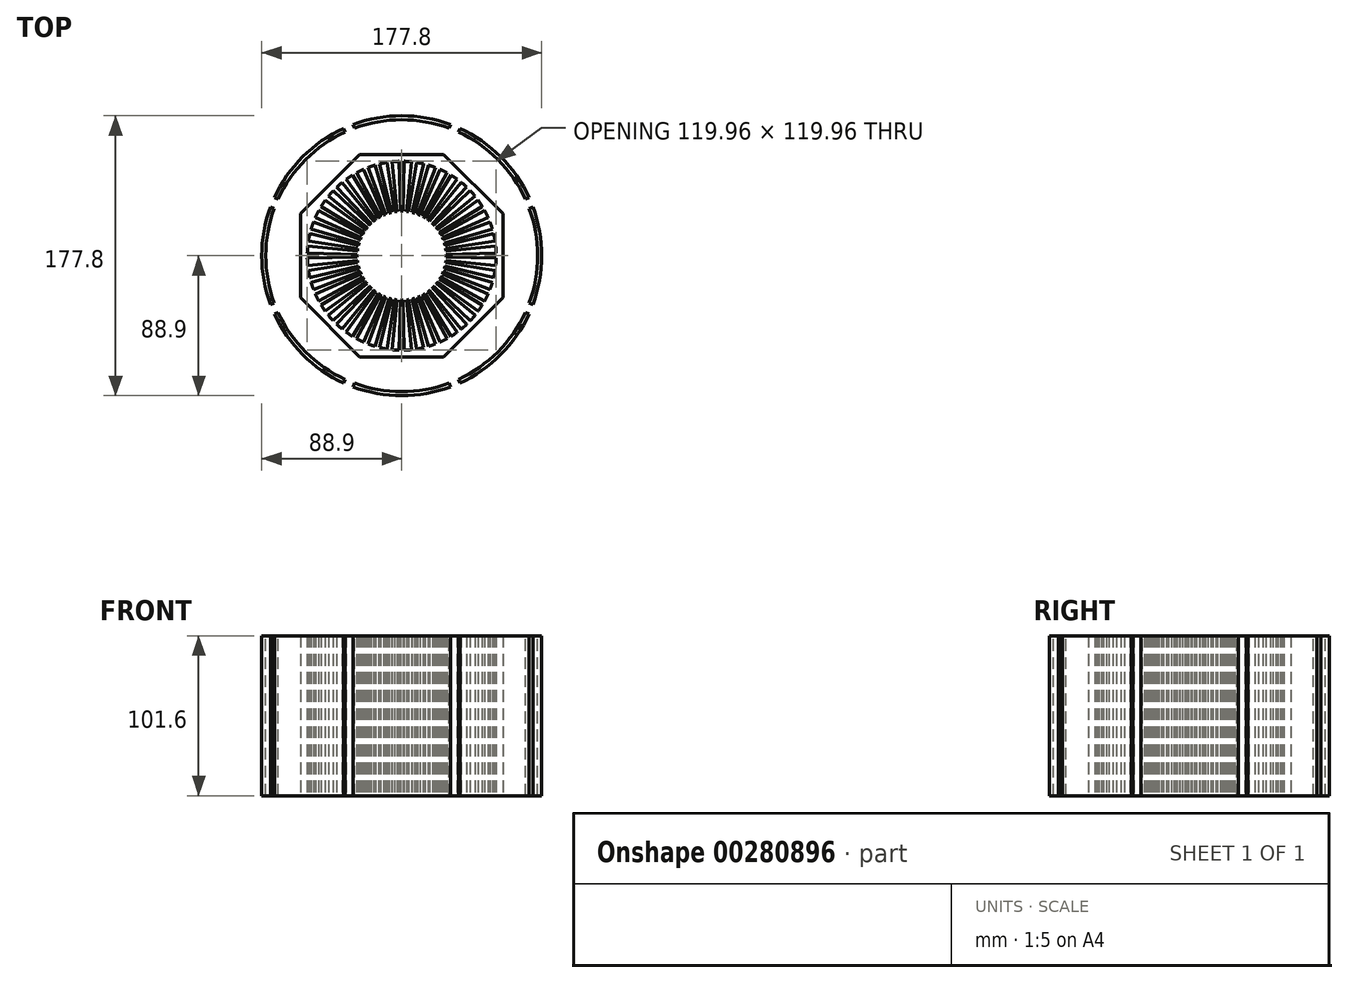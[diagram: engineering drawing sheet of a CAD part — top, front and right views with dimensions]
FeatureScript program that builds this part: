
annotation { "Feature Type Name" : "Feature", "Feature Type Description" : "" }
export const myFeature = defineFeature(function(context is Context, id is Id, definition is map)
    precondition{}
    {
        {
            var Q0;
            Q0=qCreatedBy(makeId("Top.planeOp"),FACE);
            var sketch = newSketch(context, id + "F0", { "sketchPlane" : qUnion([Q0])});
            skCircle(sketch, "E0", {"center": v(0, 0) * mm, "radius": 60 * mm});
            skCircle(sketch, "E1", {"center": v(0, 0) * mm, "radius": 457.2 * mm, "construction": true});
            skCircle(sketch, "E2.cCircle", {"center": v(0, 0) * mm, "radius": 64.39 * mm, "construction": true});
            skLineSegment(sketch, "E2.0", {"start": v(26.67, -64.39) * mm, "end": v(-26.67, -64.39) * mm});
            skLineSegment(sketch, "E2.1", {"start": v(-26.67, -64.39) * mm, "end": v(-64.39, -26.67) * mm});
            skLineSegment(sketch, "E2.2", {"start": v(-64.39, -26.67) * mm, "end": v(-64.39, 26.67) * mm});
            skLineSegment(sketch, "E2.3", {"start": v(-64.39, 26.67) * mm, "end": v(-26.67, 64.39) * mm});
            skLineSegment(sketch, "E2.4", {"start": v(-26.67, 64.39) * mm, "end": v(26.67, 64.39) * mm});
            skLineSegment(sketch, "E2.5", {"start": v(26.67, 64.39) * mm, "end": v(64.39, 26.67) * mm});
            skLineSegment(sketch, "E2.6", {"start": v(64.39, 26.67) * mm, "end": v(64.39, -26.67) * mm});
            skLineSegment(sketch, "E2.7", {"start": v(64.39, -26.67) * mm, "end": v(26.67, -64.39) * mm});
            skPoint(sketch, "E2.0.midPoint", {"position": v(0, -64.39) * mm});
            skLineSegment(sketch, "E3", {"start": v(0, 64.39) * mm, "end": v(0, 64.39) * mm});
            skPoint(sketch, "E3.endSnap0", {"position": v(0, 64.39) * mm});
            skPoint(sketch, "E4", {"position": v(-6.6, 64.39) * mm});
            skLineSegment(sketch, "E5", {"start": v(-6.6, 64.39) * mm, "end": v(-367.1, 272.52) * mm, "construction": true});
            skLineSegment(sketch, "E6.MirrorCS", {"start": v(6.6, 64.39) * mm, "end": v(367.1, 272.52) * mm, "construction": true});
            skLineSegment(sketch, "E7.bottom", {"start": v(114, -34) * mm, "end": v(-114, -34) * mm});
            skLineSegment(sketch, "E7.top", {"start": v(114, 34) * mm, "end": v(-114, 34) * mm});
            skLineSegment(sketch, "E7.left", {"start": v(114, -34) * mm, "end": v(114, 34) * mm});
            skLineSegment(sketch, "E7.right", {"start": v(-114, -34) * mm, "end": v(-114, 34) * mm});
            skCircle(sketch, "E8", {"center": v(0, 0) * mm, "radius": 88.9 * mm});
            skLineSegment(sketch, "E9", {"start": v(-26.67, 64.39) * mm, "end": v(-50.86, 122.8) * mm, "construction": true});
            skLineSegment(sketch, "E10.1.0", {"start": v(-50.2, 40.86) * mm, "end": v(-452.28, -66.88) * mm, "construction": true});
            skLineSegment(sketch, "E10.1.1", {"start": v(-40.86, 50.2) * mm, "end": v(66.88, 452.28) * mm, "construction": true});
            skLineSegment(sketch, "E10.2.0", {"start": v(-64.39, -6.6) * mm, "end": v(-272.52, -367.1) * mm, "construction": true});
            skLineSegment(sketch, "E10.2.1", {"start": v(-64.39, 6.6) * mm, "end": v(-272.52, 367.1) * mm, "construction": true});
            skLineSegment(sketch, "E10.3.0", {"start": v(-40.86, -50.2) * mm, "end": v(66.88, -452.28) * mm, "construction": true});
            skLineSegment(sketch, "E10.3.1", {"start": v(-50.2, -40.86) * mm, "end": v(-452.28, 66.88) * mm, "construction": true});
            skLineSegment(sketch, "E10.4.0", {"start": v(6.6, -64.39) * mm, "end": v(367.1, -272.52) * mm, "construction": true});
            skLineSegment(sketch, "E10.4.1", {"start": v(-6.6, -64.39) * mm, "end": v(-367.1, -272.52) * mm, "construction": true});
            skLineSegment(sketch, "E10.5.0", {"start": v(50.2, -40.86) * mm, "end": v(452.28, 66.88) * mm, "construction": true});
            skLineSegment(sketch, "E10.5.1", {"start": v(40.86, -50.2) * mm, "end": v(-66.88, -452.28) * mm, "construction": true});
            skLineSegment(sketch, "E10.6.0", {"start": v(64.39, 6.6) * mm, "end": v(272.52, 367.1) * mm, "construction": true});
            skLineSegment(sketch, "E10.6.1", {"start": v(64.39, -6.6) * mm, "end": v(272.52, -367.1) * mm, "construction": true});
            skLineSegment(sketch, "E10.7.0", {"start": v(40.86, 50.2) * mm, "end": v(-66.88, 452.28) * mm, "construction": true});
            skLineSegment(sketch, "E10.7.1", {"start": v(50.2, 40.86) * mm, "end": v(452.28, -66.88) * mm, "construction": true});
            skPoint(sketch, "E11", {"position": v(-32.98, 79.62) * mm});
            skLineSegment(sketch, "E12", {"start": v(0, -64.39) * mm, "end": v(0, -133.64) * mm, "construction": true});
            skSolve(sketch);
        }
        {
            var Q0;
            Q0=qCreatedBy(makeId("Top.planeOp"),FACE);
            var sketch = newSketch(context, id + "F1", { "sketchPlane" : qUnion([Q0])});
            skLineSegment(sketch, "E13.0", {"start": v(-26.67, 64.39) * mm, "end": v(26.67, 64.39) * mm});
            skLineSegment(sketch, "E14.0", {"start": v(-64.39, 26.67) * mm, "end": v(-26.67, 64.39) * mm});
            skLineSegment(sketch, "E15.0", {"start": v(-64.39, -26.67) * mm, "end": v(-64.39, 26.67) * mm});
            skLineSegment(sketch, "E16.0", {"start": v(-26.67, -64.39) * mm, "end": v(-64.39, -26.67) * mm});
            skLineSegment(sketch, "E17.0", {"start": v(26.67, -64.39) * mm, "end": v(-26.67, -64.39) * mm});
            skLineSegment(sketch, "E18.0", {"start": v(64.39, -26.67) * mm, "end": v(26.67, -64.39) * mm});
            skLineSegment(sketch, "E19.0", {"start": v(64.39, 26.67) * mm, "end": v(64.39, -26.67) * mm});
            skLineSegment(sketch, "E20.0", {"start": v(26.67, 64.39) * mm, "end": v(64.39, 26.67) * mm});
            skCircle(sketch, "E21.0", {"center": v(0, 0) * mm, "radius": 60 * mm});
            skSolve(sketch);
        }
        {
            var Q0;
            Q0 = qSketchRegion(id + "F1", true);
            extrude(context, id + "F2", {"entities" : qUnion([Q0]), "endBound" : BoundingType.SYMMETRIC, "depth" : 101.6 * mm});
        }
        {
            var Q0;
            Q0=qCreatedBy(makeId("Top.planeOp"),FACE);
            var sketch = newSketch(context, id + "F3", { "sketchPlane" : qUnion([Q0])});
            skArc(sketch, "E22", {"start": v(0.74, 28.24) * mm, "mid": v(0, 28.25) * mm, "end": v(-0.74, 28.24) * mm});
            skArc(sketch, "E23.0", {"start": v(1.57, 59.98) * mm, "mid": v(0, 60) * mm, "end": v(-1.57, 59.98) * mm});
            skLineSegment(sketch, "E24", {"start": v(0, 0) * mm, "end": v(0, 69.36) * mm, "construction": true});
            skLineSegment(sketch, "E25", {"start": v(-0.74, 28.24) * mm, "end": v(-1.57, 59.98) * mm});
            skLineSegment(sketch, "E26.MirrorCS", {"start": v(0.74, 28.24) * mm, "end": v(1.57, 59.98) * mm});
            skLineSegment(sketch, "E27.1.0", {"start": v(-4.42, 27.9) * mm, "end": v(-9.39, 59.26) * mm});
            skLineSegment(sketch, "E27.1.1", {"start": v(-2.95, 28.1) * mm, "end": v(-6.27, 59.67) * mm});
            skArc(sketch, "E27.1.2", {"start": v(-2.95, 28.1) * mm, "mid": v(-3.69, 28) * mm, "end": v(-4.42, 27.9) * mm});
            skArc(sketch, "E27.1.3", {"start": v(-6.27, 59.67) * mm, "mid": v(-7.83, 59.49) * mm, "end": v(-9.39, 59.26) * mm});
            skLineSegment(sketch, "E27.2.0", {"start": v(-8.02, 27.09) * mm, "end": v(-17.04, 57.53) * mm});
            skLineSegment(sketch, "E27.2.1", {"start": v(-6.6, 27.47) * mm, "end": v(-14, 58.34) * mm});
            skArc(sketch, "E27.2.2", {"start": v(-6.6, 27.47) * mm, "mid": v(-7.31, 27.29) * mm, "end": v(-8.02, 27.09) * mm});
            skArc(sketch, "E27.2.3", {"start": v(-14, 58.34) * mm, "mid": v(-15.53, 57.96) * mm, "end": v(-17.04, 57.53) * mm});
            skLineSegment(sketch, "E27.3.0", {"start": v(-11.5, 25.8) * mm, "end": v(-24.4, 54.81) * mm});
            skLineSegment(sketch, "E27.3.1", {"start": v(-10.12, 26.37) * mm, "end": v(-21.5, 56.01) * mm});
            skArc(sketch, "E27.3.2", {"start": v(-10.12, 26.37) * mm, "mid": v(-10.81, 26.1) * mm, "end": v(-11.5, 25.8) * mm});
            skArc(sketch, "E27.3.3", {"start": v(-21.5, 56.01) * mm, "mid": v(-22.96, 55.43) * mm, "end": v(-24.4, 54.81) * mm});
            skLineSegment(sketch, "E27.4.0", {"start": v(-14.76, 24.09) * mm, "end": v(-31.35, 51.16) * mm});
            skLineSegment(sketch, "E27.4.1", {"start": v(-13.48, 24.83) * mm, "end": v(-28.63, 52.73) * mm});
            skArc(sketch, "E27.4.2", {"start": v(-13.48, 24.83) * mm, "mid": v(-14.13, 24.47) * mm, "end": v(-14.76, 24.09) * mm});
            skArc(sketch, "E27.4.3", {"start": v(-28.63, 52.73) * mm, "mid": v(-30, 51.96) * mm, "end": v(-31.35, 51.16) * mm});
            skLineSegment(sketch, "E27.5.0", {"start": v(-17.78, 21.95) * mm, "end": v(-37.76, 46.63) * mm});
            skLineSegment(sketch, "E27.5.1", {"start": v(-16.6, 22.85) * mm, "end": v(-35.27, 48.54) * mm});
            skArc(sketch, "E27.5.2", {"start": v(-16.6, 22.85) * mm, "mid": v(-17.2, 22.41) * mm, "end": v(-17.78, 21.95) * mm});
            skArc(sketch, "E27.5.3", {"start": v(-35.27, 48.54) * mm, "mid": v(-36.53, 47.6) * mm, "end": v(-37.76, 46.63) * mm});
            skLineSegment(sketch, "E27.6.0", {"start": v(-20.5, 19.45) * mm, "end": v(-43.52, 41.3) * mm});
            skLineSegment(sketch, "E27.6.1", {"start": v(-19.45, 20.5) * mm, "end": v(-41.3, 43.52) * mm});
            skArc(sketch, "E27.6.2", {"start": v(-19.45, 20.5) * mm, "mid": v(-19.98, 19.98) * mm, "end": v(-20.5, 19.45) * mm});
            skArc(sketch, "E27.6.3", {"start": v(-41.3, 43.52) * mm, "mid": v(-42.43, 42.43) * mm, "end": v(-43.52, 41.3) * mm});
            skLineSegment(sketch, "E27.7.0", {"start": v(-22.85, 16.6) * mm, "end": v(-48.54, 35.27) * mm});
            skLineSegment(sketch, "E27.7.1", {"start": v(-21.95, 17.78) * mm, "end": v(-46.63, 37.76) * mm});
            skArc(sketch, "E27.7.2", {"start": v(-21.95, 17.78) * mm, "mid": v(-22.41, 17.2) * mm, "end": v(-22.85, 16.6) * mm});
            skArc(sketch, "E27.7.3", {"start": v(-46.63, 37.76) * mm, "mid": v(-47.6, 36.53) * mm, "end": v(-48.54, 35.27) * mm});
            skLineSegment(sketch, "E27.8.0", {"start": v(-24.83, 13.48) * mm, "end": v(-52.73, 28.63) * mm});
            skLineSegment(sketch, "E27.8.1", {"start": v(-24.09, 14.76) * mm, "end": v(-51.16, 31.35) * mm});
            skArc(sketch, "E27.8.2", {"start": v(-24.09, 14.76) * mm, "mid": v(-24.47, 14.12) * mm, "end": v(-24.83, 13.48) * mm});
            skArc(sketch, "E27.8.3", {"start": v(-51.16, 31.35) * mm, "mid": v(-51.96, 30) * mm, "end": v(-52.73, 28.63) * mm});
            skLineSegment(sketch, "E27.9.0", {"start": v(-26.37, 10.12) * mm, "end": v(-56.01, 21.5) * mm});
            skLineSegment(sketch, "E27.9.1", {"start": v(-25.8, 11.5) * mm, "end": v(-54.81, 24.4) * mm});
            skArc(sketch, "E27.9.2", {"start": v(-25.8, 11.5) * mm, "mid": v(-26.1, 10.81) * mm, "end": v(-26.37, 10.12) * mm});
            skArc(sketch, "E27.9.3", {"start": v(-54.81, 24.4) * mm, "mid": v(-55.43, 22.96) * mm, "end": v(-56.01, 21.5) * mm});
            skLineSegment(sketch, "E27.10.0", {"start": v(-27.47, 6.6) * mm, "end": v(-58.34, 14) * mm});
            skLineSegment(sketch, "E27.10.1", {"start": v(-27.09, 8.02) * mm, "end": v(-57.53, 17.04) * mm});
            skArc(sketch, "E27.10.2", {"start": v(-27.09, 8.02) * mm, "mid": v(-27.29, 7.31) * mm, "end": v(-27.47, 6.6) * mm});
            skArc(sketch, "E27.10.3", {"start": v(-57.53, 17.04) * mm, "mid": v(-57.96, 15.53) * mm, "end": v(-58.34, 14) * mm});
            skLineSegment(sketch, "E27.11.0", {"start": v(-28.1, 2.95) * mm, "end": v(-59.67, 6.27) * mm});
            skLineSegment(sketch, "E27.11.1", {"start": v(-27.9, 4.42) * mm, "end": v(-59.26, 9.39) * mm});
            skArc(sketch, "E27.11.2", {"start": v(-27.9, 4.42) * mm, "mid": v(-28, 3.69) * mm, "end": v(-28.1, 2.95) * mm});
            skArc(sketch, "E27.11.3", {"start": v(-59.26, 9.39) * mm, "mid": v(-59.49, 7.83) * mm, "end": v(-59.67, 6.27) * mm});
            skLineSegment(sketch, "E27.12.0", {"start": v(-28.24, -0.74) * mm, "end": v(-59.98, -1.57) * mm});
            skLineSegment(sketch, "E27.12.1", {"start": v(-28.24, 0.74) * mm, "end": v(-59.98, 1.57) * mm});
            skArc(sketch, "E27.12.2", {"start": v(-28.24, 0.74) * mm, "mid": v(-28.25, 0) * mm, "end": v(-28.24, -0.74) * mm});
            skArc(sketch, "E27.12.3", {"start": v(-59.98, 1.57) * mm, "mid": v(-60, 0) * mm, "end": v(-59.98, -1.57) * mm});
            skLineSegment(sketch, "E27.13.0", {"start": v(-27.9, -4.42) * mm, "end": v(-59.26, -9.39) * mm});
            skLineSegment(sketch, "E27.13.1", {"start": v(-28.1, -2.95) * mm, "end": v(-59.67, -6.27) * mm});
            skArc(sketch, "E27.13.2", {"start": v(-28.1, -2.95) * mm, "mid": v(-28, -3.69) * mm, "end": v(-27.9, -4.42) * mm});
            skArc(sketch, "E27.13.3", {"start": v(-59.67, -6.27) * mm, "mid": v(-59.49, -7.83) * mm, "end": v(-59.26, -9.39) * mm});
            skLineSegment(sketch, "E27.14.0", {"start": v(-27.09, -8.02) * mm, "end": v(-57.53, -17.04) * mm});
            skLineSegment(sketch, "E27.14.1", {"start": v(-27.47, -6.6) * mm, "end": v(-58.34, -14) * mm});
            skArc(sketch, "E27.14.2", {"start": v(-27.47, -6.6) * mm, "mid": v(-27.29, -7.31) * mm, "end": v(-27.09, -8.02) * mm});
            skArc(sketch, "E27.14.3", {"start": v(-58.34, -14) * mm, "mid": v(-57.96, -15.53) * mm, "end": v(-57.53, -17.04) * mm});
            skLineSegment(sketch, "E27.15.0", {"start": v(-25.8, -11.5) * mm, "end": v(-54.81, -24.4) * mm});
            skLineSegment(sketch, "E27.15.1", {"start": v(-26.37, -10.12) * mm, "end": v(-56.01, -21.5) * mm});
            skArc(sketch, "E27.15.2", {"start": v(-26.37, -10.12) * mm, "mid": v(-26.1, -10.81) * mm, "end": v(-25.8, -11.5) * mm});
            skArc(sketch, "E27.15.3", {"start": v(-56.01, -21.5) * mm, "mid": v(-55.43, -22.96) * mm, "end": v(-54.81, -24.4) * mm});
            skLineSegment(sketch, "E27.16.0", {"start": v(-24.09, -14.76) * mm, "end": v(-51.16, -31.35) * mm});
            skLineSegment(sketch, "E27.16.1", {"start": v(-24.83, -13.48) * mm, "end": v(-52.73, -28.63) * mm});
            skArc(sketch, "E27.16.2", {"start": v(-24.83, -13.48) * mm, "mid": v(-24.47, -14.13) * mm, "end": v(-24.09, -14.76) * mm});
            skArc(sketch, "E27.16.3", {"start": v(-52.73, -28.63) * mm, "mid": v(-51.96, -30) * mm, "end": v(-51.16, -31.35) * mm});
            skLineSegment(sketch, "E27.17.0", {"start": v(-21.95, -17.78) * mm, "end": v(-46.63, -37.76) * mm});
            skLineSegment(sketch, "E27.17.1", {"start": v(-22.85, -16.6) * mm, "end": v(-48.54, -35.27) * mm});
            skArc(sketch, "E27.17.2", {"start": v(-22.85, -16.6) * mm, "mid": v(-22.41, -17.2) * mm, "end": v(-21.95, -17.78) * mm});
            skArc(sketch, "E27.17.3", {"start": v(-48.54, -35.27) * mm, "mid": v(-47.6, -36.53) * mm, "end": v(-46.63, -37.76) * mm});
            skLineSegment(sketch, "E27.18.0", {"start": v(-19.45, -20.5) * mm, "end": v(-41.3, -43.52) * mm});
            skLineSegment(sketch, "E27.18.1", {"start": v(-20.5, -19.45) * mm, "end": v(-43.52, -41.3) * mm});
            skArc(sketch, "E27.18.2", {"start": v(-20.5, -19.45) * mm, "mid": v(-19.98, -19.98) * mm, "end": v(-19.45, -20.5) * mm});
            skArc(sketch, "E27.18.3", {"start": v(-43.52, -41.3) * mm, "mid": v(-42.43, -42.43) * mm, "end": v(-41.3, -43.52) * mm});
            skLineSegment(sketch, "E27.19.0", {"start": v(-16.6, -22.85) * mm, "end": v(-35.27, -48.54) * mm});
            skLineSegment(sketch, "E27.19.1", {"start": v(-17.78, -21.95) * mm, "end": v(-37.76, -46.63) * mm});
            skArc(sketch, "E27.19.2", {"start": v(-17.78, -21.95) * mm, "mid": v(-17.2, -22.41) * mm, "end": v(-16.6, -22.85) * mm});
            skArc(sketch, "E27.19.3", {"start": v(-37.76, -46.63) * mm, "mid": v(-36.53, -47.6) * mm, "end": v(-35.27, -48.54) * mm});
            skLineSegment(sketch, "E27.20.0", {"start": v(-13.48, -24.83) * mm, "end": v(-28.63, -52.73) * mm});
            skLineSegment(sketch, "E27.20.1", {"start": v(-14.76, -24.09) * mm, "end": v(-31.35, -51.16) * mm});
            skArc(sketch, "E27.20.2", {"start": v(-14.76, -24.09) * mm, "mid": v(-14.12, -24.47) * mm, "end": v(-13.48, -24.83) * mm});
            skArc(sketch, "E27.20.3", {"start": v(-31.35, -51.16) * mm, "mid": v(-30, -51.96) * mm, "end": v(-28.63, -52.73) * mm});
            skLineSegment(sketch, "E27.21.0", {"start": v(-10.12, -26.37) * mm, "end": v(-21.5, -56.01) * mm});
            skLineSegment(sketch, "E27.21.1", {"start": v(-11.5, -25.8) * mm, "end": v(-24.4, -54.81) * mm});
            skArc(sketch, "E27.21.2", {"start": v(-11.5, -25.8) * mm, "mid": v(-10.81, -26.1) * mm, "end": v(-10.12, -26.37) * mm});
            skArc(sketch, "E27.21.3", {"start": v(-24.4, -54.81) * mm, "mid": v(-22.96, -55.43) * mm, "end": v(-21.5, -56.01) * mm});
            skLineSegment(sketch, "E27.22.0", {"start": v(-6.6, -27.47) * mm, "end": v(-14, -58.34) * mm});
            skLineSegment(sketch, "E27.22.1", {"start": v(-8.02, -27.09) * mm, "end": v(-17.04, -57.53) * mm});
            skArc(sketch, "E27.22.2", {"start": v(-8.02, -27.09) * mm, "mid": v(-7.31, -27.29) * mm, "end": v(-6.6, -27.47) * mm});
            skArc(sketch, "E27.22.3", {"start": v(-17.04, -57.53) * mm, "mid": v(-15.53, -57.96) * mm, "end": v(-14, -58.34) * mm});
            skLineSegment(sketch, "E27.23.0", {"start": v(-2.95, -28.1) * mm, "end": v(-6.27, -59.67) * mm});
            skLineSegment(sketch, "E27.23.1", {"start": v(-4.42, -27.9) * mm, "end": v(-9.39, -59.26) * mm});
            skArc(sketch, "E27.23.2", {"start": v(-4.42, -27.9) * mm, "mid": v(-3.69, -28) * mm, "end": v(-2.95, -28.1) * mm});
            skArc(sketch, "E27.23.3", {"start": v(-9.39, -59.26) * mm, "mid": v(-7.83, -59.49) * mm, "end": v(-6.27, -59.67) * mm});
            skLineSegment(sketch, "E27.24.0", {"start": v(0.74, -28.24) * mm, "end": v(1.57, -59.98) * mm});
            skLineSegment(sketch, "E27.24.1", {"start": v(-0.74, -28.24) * mm, "end": v(-1.57, -59.98) * mm});
            skArc(sketch, "E27.24.2", {"start": v(-0.74, -28.24) * mm, "mid": v(0, -28.25) * mm, "end": v(0.74, -28.24) * mm});
            skArc(sketch, "E27.24.3", {"start": v(-1.57, -59.98) * mm, "mid": v(0, -60) * mm, "end": v(1.57, -59.98) * mm});
            skLineSegment(sketch, "E27.25.0", {"start": v(4.42, -27.9) * mm, "end": v(9.39, -59.26) * mm});
            skLineSegment(sketch, "E27.25.1", {"start": v(2.95, -28.1) * mm, "end": v(6.27, -59.67) * mm});
            skArc(sketch, "E27.25.2", {"start": v(2.95, -28.1) * mm, "mid": v(3.69, -28) * mm, "end": v(4.42, -27.9) * mm});
            skArc(sketch, "E27.25.3", {"start": v(6.27, -59.67) * mm, "mid": v(7.83, -59.49) * mm, "end": v(9.39, -59.26) * mm});
            skLineSegment(sketch, "E27.26.0", {"start": v(8.02, -27.09) * mm, "end": v(17.04, -57.53) * mm});
            skLineSegment(sketch, "E27.26.1", {"start": v(6.6, -27.47) * mm, "end": v(14, -58.34) * mm});
            skArc(sketch, "E27.26.2", {"start": v(6.6, -27.47) * mm, "mid": v(7.31, -27.29) * mm, "end": v(8.02, -27.09) * mm});
            skArc(sketch, "E27.26.3", {"start": v(14, -58.34) * mm, "mid": v(15.53, -57.96) * mm, "end": v(17.04, -57.53) * mm});
            skLineSegment(sketch, "E27.27.0", {"start": v(11.5, -25.8) * mm, "end": v(24.4, -54.81) * mm});
            skLineSegment(sketch, "E27.27.1", {"start": v(10.12, -26.37) * mm, "end": v(21.5, -56.01) * mm});
            skArc(sketch, "E27.27.2", {"start": v(10.12, -26.37) * mm, "mid": v(10.81, -26.1) * mm, "end": v(11.5, -25.8) * mm});
            skArc(sketch, "E27.27.3", {"start": v(21.5, -56.01) * mm, "mid": v(22.96, -55.43) * mm, "end": v(24.4, -54.81) * mm});
            skLineSegment(sketch, "E27.28.0", {"start": v(14.76, -24.09) * mm, "end": v(31.35, -51.16) * mm});
            skLineSegment(sketch, "E27.28.1", {"start": v(13.48, -24.83) * mm, "end": v(28.63, -52.73) * mm});
            skArc(sketch, "E27.28.2", {"start": v(13.48, -24.83) * mm, "mid": v(14.13, -24.47) * mm, "end": v(14.76, -24.09) * mm});
            skArc(sketch, "E27.28.3", {"start": v(28.63, -52.73) * mm, "mid": v(30, -51.96) * mm, "end": v(31.35, -51.16) * mm});
            skLineSegment(sketch, "E27.29.0", {"start": v(17.78, -21.95) * mm, "end": v(37.76, -46.63) * mm});
            skLineSegment(sketch, "E27.29.1", {"start": v(16.6, -22.85) * mm, "end": v(35.27, -48.54) * mm});
            skArc(sketch, "E27.29.2", {"start": v(16.6, -22.85) * mm, "mid": v(17.2, -22.41) * mm, "end": v(17.78, -21.95) * mm});
            skArc(sketch, "E27.29.3", {"start": v(35.27, -48.54) * mm, "mid": v(36.53, -47.6) * mm, "end": v(37.76, -46.63) * mm});
            skLineSegment(sketch, "E27.30.0", {"start": v(20.5, -19.45) * mm, "end": v(43.52, -41.3) * mm});
            skLineSegment(sketch, "E27.30.1", {"start": v(19.45, -20.5) * mm, "end": v(41.3, -43.52) * mm});
            skArc(sketch, "E27.30.2", {"start": v(19.45, -20.5) * mm, "mid": v(19.98, -19.98) * mm, "end": v(20.5, -19.45) * mm});
            skArc(sketch, "E27.30.3", {"start": v(41.3, -43.52) * mm, "mid": v(42.43, -42.43) * mm, "end": v(43.52, -41.3) * mm});
            skLineSegment(sketch, "E27.31.0", {"start": v(22.85, -16.6) * mm, "end": v(48.54, -35.27) * mm});
            skLineSegment(sketch, "E27.31.1", {"start": v(21.95, -17.78) * mm, "end": v(46.63, -37.76) * mm});
            skArc(sketch, "E27.31.2", {"start": v(21.95, -17.78) * mm, "mid": v(22.41, -17.2) * mm, "end": v(22.85, -16.6) * mm});
            skArc(sketch, "E27.31.3", {"start": v(46.63, -37.76) * mm, "mid": v(47.6, -36.53) * mm, "end": v(48.54, -35.27) * mm});
            skLineSegment(sketch, "E27.32.0", {"start": v(24.83, -13.48) * mm, "end": v(52.73, -28.63) * mm});
            skLineSegment(sketch, "E27.32.1", {"start": v(24.09, -14.76) * mm, "end": v(51.16, -31.35) * mm});
            skArc(sketch, "E27.32.2", {"start": v(24.09, -14.76) * mm, "mid": v(24.47, -14.13) * mm, "end": v(24.83, -13.48) * mm});
            skArc(sketch, "E27.32.3", {"start": v(51.16, -31.35) * mm, "mid": v(51.96, -30) * mm, "end": v(52.73, -28.63) * mm});
            skLineSegment(sketch, "E27.33.0", {"start": v(26.37, -10.12) * mm, "end": v(56.01, -21.5) * mm});
            skLineSegment(sketch, "E27.33.1", {"start": v(25.8, -11.5) * mm, "end": v(54.81, -24.4) * mm});
            skArc(sketch, "E27.33.2", {"start": v(25.8, -11.5) * mm, "mid": v(26.1, -10.81) * mm, "end": v(26.37, -10.12) * mm});
            skArc(sketch, "E27.33.3", {"start": v(54.81, -24.4) * mm, "mid": v(55.43, -22.96) * mm, "end": v(56.01, -21.5) * mm});
            skLineSegment(sketch, "E27.34.0", {"start": v(27.47, -6.6) * mm, "end": v(58.34, -14) * mm});
            skLineSegment(sketch, "E27.34.1", {"start": v(27.09, -8.02) * mm, "end": v(57.53, -17.04) * mm});
            skArc(sketch, "E27.34.2", {"start": v(27.09, -8.02) * mm, "mid": v(27.29, -7.31) * mm, "end": v(27.47, -6.6) * mm});
            skArc(sketch, "E27.34.3", {"start": v(57.53, -17.04) * mm, "mid": v(57.96, -15.53) * mm, "end": v(58.34, -14) * mm});
            skLineSegment(sketch, "E27.35.0", {"start": v(28.1, -2.95) * mm, "end": v(59.67, -6.27) * mm});
            skLineSegment(sketch, "E27.35.1", {"start": v(27.9, -4.42) * mm, "end": v(59.26, -9.39) * mm});
            skArc(sketch, "E27.35.2", {"start": v(27.9, -4.42) * mm, "mid": v(28, -3.69) * mm, "end": v(28.1, -2.95) * mm});
            skArc(sketch, "E27.35.3", {"start": v(59.26, -9.39) * mm, "mid": v(59.49, -7.83) * mm, "end": v(59.67, -6.27) * mm});
            skLineSegment(sketch, "E27.36.0", {"start": v(28.24, 0.74) * mm, "end": v(59.98, 1.57) * mm});
            skLineSegment(sketch, "E27.36.1", {"start": v(28.24, -0.74) * mm, "end": v(59.98, -1.57) * mm});
            skArc(sketch, "E27.36.2", {"start": v(28.24, -0.74) * mm, "mid": v(28.25, 0) * mm, "end": v(28.24, 0.74) * mm});
            skArc(sketch, "E27.36.3", {"start": v(59.98, -1.57) * mm, "mid": v(60, 0) * mm, "end": v(59.98, 1.57) * mm});
            skLineSegment(sketch, "E27.37.0", {"start": v(27.9, 4.42) * mm, "end": v(59.26, 9.39) * mm});
            skLineSegment(sketch, "E27.37.1", {"start": v(28.1, 2.95) * mm, "end": v(59.67, 6.27) * mm});
            skArc(sketch, "E27.37.2", {"start": v(28.1, 2.95) * mm, "mid": v(28, 3.69) * mm, "end": v(27.9, 4.42) * mm});
            skArc(sketch, "E27.37.3", {"start": v(59.67, 6.27) * mm, "mid": v(59.49, 7.83) * mm, "end": v(59.26, 9.39) * mm});
            skLineSegment(sketch, "E27.38.0", {"start": v(27.09, 8.02) * mm, "end": v(57.53, 17.04) * mm});
            skLineSegment(sketch, "E27.38.1", {"start": v(27.47, 6.6) * mm, "end": v(58.34, 14) * mm});
            skArc(sketch, "E27.38.2", {"start": v(27.47, 6.6) * mm, "mid": v(27.29, 7.31) * mm, "end": v(27.09, 8.02) * mm});
            skArc(sketch, "E27.38.3", {"start": v(58.34, 14) * mm, "mid": v(57.96, 15.53) * mm, "end": v(57.53, 17.04) * mm});
            skLineSegment(sketch, "E27.39.0", {"start": v(25.8, 11.5) * mm, "end": v(54.81, 24.4) * mm});
            skLineSegment(sketch, "E27.39.1", {"start": v(26.37, 10.12) * mm, "end": v(56.01, 21.5) * mm});
            skArc(sketch, "E27.39.2", {"start": v(26.37, 10.12) * mm, "mid": v(26.1, 10.81) * mm, "end": v(25.8, 11.5) * mm});
            skArc(sketch, "E27.39.3", {"start": v(56.01, 21.5) * mm, "mid": v(55.43, 22.96) * mm, "end": v(54.81, 24.4) * mm});
            skLineSegment(sketch, "E27.40.0", {"start": v(24.09, 14.76) * mm, "end": v(51.16, 31.35) * mm});
            skLineSegment(sketch, "E27.40.1", {"start": v(24.83, 13.48) * mm, "end": v(52.73, 28.63) * mm});
            skArc(sketch, "E27.40.2", {"start": v(24.83, 13.48) * mm, "mid": v(24.47, 14.12) * mm, "end": v(24.09, 14.76) * mm});
            skArc(sketch, "E27.40.3", {"start": v(52.73, 28.63) * mm, "mid": v(51.96, 30) * mm, "end": v(51.16, 31.35) * mm});
            skLineSegment(sketch, "E27.41.0", {"start": v(21.95, 17.78) * mm, "end": v(46.63, 37.76) * mm});
            skLineSegment(sketch, "E27.41.1", {"start": v(22.85, 16.6) * mm, "end": v(48.54, 35.27) * mm});
            skArc(sketch, "E27.41.2", {"start": v(22.85, 16.6) * mm, "mid": v(22.41, 17.2) * mm, "end": v(21.95, 17.78) * mm});
            skArc(sketch, "E27.41.3", {"start": v(48.54, 35.27) * mm, "mid": v(47.6, 36.53) * mm, "end": v(46.63, 37.76) * mm});
            skLineSegment(sketch, "E27.42.0", {"start": v(19.45, 20.5) * mm, "end": v(41.3, 43.52) * mm});
            skLineSegment(sketch, "E27.42.1", {"start": v(20.5, 19.45) * mm, "end": v(43.52, 41.3) * mm});
            skArc(sketch, "E27.42.2", {"start": v(20.5, 19.45) * mm, "mid": v(19.98, 19.98) * mm, "end": v(19.45, 20.5) * mm});
            skArc(sketch, "E27.42.3", {"start": v(43.52, 41.3) * mm, "mid": v(42.43, 42.43) * mm, "end": v(41.3, 43.52) * mm});
            skLineSegment(sketch, "E27.43.0", {"start": v(16.6, 22.85) * mm, "end": v(35.27, 48.54) * mm});
            skLineSegment(sketch, "E27.43.1", {"start": v(17.78, 21.95) * mm, "end": v(37.76, 46.63) * mm});
            skArc(sketch, "E27.43.2", {"start": v(17.78, 21.95) * mm, "mid": v(17.2, 22.41) * mm, "end": v(16.6, 22.85) * mm});
            skArc(sketch, "E27.43.3", {"start": v(37.76, 46.63) * mm, "mid": v(36.53, 47.6) * mm, "end": v(35.27, 48.54) * mm});
            skLineSegment(sketch, "E27.44.0", {"start": v(13.48, 24.83) * mm, "end": v(28.63, 52.73) * mm});
            skLineSegment(sketch, "E27.44.1", {"start": v(14.76, 24.09) * mm, "end": v(31.35, 51.16) * mm});
            skArc(sketch, "E27.44.2", {"start": v(14.76, 24.09) * mm, "mid": v(14.13, 24.47) * mm, "end": v(13.48, 24.83) * mm});
            skArc(sketch, "E27.44.3", {"start": v(31.35, 51.16) * mm, "mid": v(30, 51.96) * mm, "end": v(28.63, 52.73) * mm});
            skLineSegment(sketch, "E27.45.0", {"start": v(10.12, 26.37) * mm, "end": v(21.5, 56.01) * mm});
            skLineSegment(sketch, "E27.45.1", {"start": v(11.5, 25.8) * mm, "end": v(24.4, 54.81) * mm});
            skArc(sketch, "E27.45.2", {"start": v(11.5, 25.8) * mm, "mid": v(10.81, 26.1) * mm, "end": v(10.12, 26.37) * mm});
            skArc(sketch, "E27.45.3", {"start": v(24.4, 54.81) * mm, "mid": v(22.96, 55.43) * mm, "end": v(21.5, 56.01) * mm});
            skLineSegment(sketch, "E27.46.0", {"start": v(6.6, 27.47) * mm, "end": v(14, 58.34) * mm});
            skLineSegment(sketch, "E27.46.1", {"start": v(8.02, 27.09) * mm, "end": v(17.04, 57.53) * mm});
            skArc(sketch, "E27.46.2", {"start": v(8.02, 27.09) * mm, "mid": v(7.31, 27.29) * mm, "end": v(6.6, 27.47) * mm});
            skArc(sketch, "E27.46.3", {"start": v(17.04, 57.53) * mm, "mid": v(15.53, 57.96) * mm, "end": v(14, 58.34) * mm});
            skLineSegment(sketch, "E27.47.0", {"start": v(2.95, 28.1) * mm, "end": v(6.27, 59.67) * mm});
            skLineSegment(sketch, "E27.47.1", {"start": v(4.42, 27.9) * mm, "end": v(9.39, 59.26) * mm});
            skArc(sketch, "E27.47.2", {"start": v(4.42, 27.9) * mm, "mid": v(3.69, 28) * mm, "end": v(2.95, 28.1) * mm});
            skArc(sketch, "E27.47.3", {"start": v(9.39, 59.26) * mm, "mid": v(7.83, 59.49) * mm, "end": v(6.27, 59.67) * mm});
            skSolve(sketch);
        }
        {
            var Q0;
            Q0 = qSketchRegion(id + "F3", true);
            var Q1;
            Q1=makeQuery(id+"F2.opExtrude","CAP_FACE",FACE,{"disambiguationData":[OSD([sQuery(id+"F1.wireOp",EDGE,"E13.0"),sQuery(id+"F1.wireOp",EDGE,"E14.0"),sQuery(id+"F1.wireOp",EDGE,"E15.0"),sQuery(id+"F1.wireOp",EDGE,"E16.0"),sQuery(id+"F1.wireOp",EDGE,"E17.0"),sQuery(id+"F1.wireOp",EDGE,"E18.0"),sQuery(id+"F1.wireOp",EDGE,"E19.0"),sQuery(id+"F1.wireOp",EDGE,"E20.0"),sQuery(id+"F1.wireOp",EDGE,"E21.0")])],"isStart":false});
            var Q2;
            Q2=makeQuery(id+"F2.opExtrude","CAP_FACE",FACE,{"disambiguationData":[OSD([sQuery(id+"F1.wireOp",EDGE,"E13.0"),sQuery(id+"F1.wireOp",EDGE,"E14.0"),sQuery(id+"F1.wireOp",EDGE,"E15.0"),sQuery(id+"F1.wireOp",EDGE,"E16.0"),sQuery(id+"F1.wireOp",EDGE,"E17.0"),sQuery(id+"F1.wireOp",EDGE,"E18.0"),sQuery(id+"F1.wireOp",EDGE,"E19.0"),sQuery(id+"F1.wireOp",EDGE,"E20.0"),sQuery(id+"F1.wireOp",EDGE,"E21.0")])],"isStart":true});
            extrude(context, id + "F4", {"entities" : qUnion([Q0]), "operationType" : NewBodyOperationType.ADD, "endBound" : BoundingType.UP_TO_SURFACE, "endBoundEntityFace" : qUnion([Q1]), "depth" : 25.4 * mm, "hasSecondDirection" : true, "secondDirectionBound" : SecondDirectionBoundingType.UP_TO_SURFACE, "secondDirectionOppositeDirection" : true, "secondDirectionBoundEntityFace" : qUnion([Q2]), "secondDirectionDepth" : 25.4 * mm});
        }
        {
            var Q0;
            Q0=qCreatedBy(makeId("Front.planeOp"),FACE);
            var sketch = newSketch(context, id + "F5", { "sketchPlane" : qUnion([Q0])});
            skLineSegment(sketch, "E28", {"start": v(0, 0) * mm, "end": v(0, 50.8) * mm, "construction": true});
            skPoint(sketch, "E29", {"position": v(0, 38.1) * mm});
            skLineSegment(sketch, "E30", {"start": v(0, 0) * mm, "end": v(166.15, 0) * mm, "construction": true});
            skPoint(sketch, "E31", {"position": v(0, 114.3) * mm});
            skPoint(sketch, "E32.MirrorP", {"position": v(0, -38.1) * mm});
            skPoint(sketch, "E33.MirrorP", {"position": v(0, -114.3) * mm});
            skSolve(sketch);
        }
        {
            var Q0;
            Q0=qCreatedBy(makeId("Top.planeOp"),FACE);
            var sketch = newSketch(context, id + "F6", { "sketchPlane" : qUnion([Q0])});
            skArc(sketch, "E34.0", {"start": v(-31.07, -83.3) * mm, "mid": v(0, -88.9) * mm, "end": v(31.07, -83.3) * mm});
            skArc(sketch, "E35", {"start": v(-30.1, -80.95) * mm, "mid": v(0, -86.36) * mm, "end": v(30.1, -80.95) * mm});
            skLineSegment(sketch, "E36", {"start": v(0, 0) * mm, "end": v(-39.4, -95.1) * mm, "construction": true});
            skLineSegment(sketch, "E37.0", {"start": v(0, -64.39) * mm, "end": v(0, -133.64) * mm, "construction": true});
            skLineSegment(sketch, "E38.MirrorCS", {"start": v(31.07, -83.3) * mm, "end": v(30.1, -80.95) * mm});
            skPoint(sketch, "E39", {"position": v(-32.98, -79.62) * mm});
            skLineSegment(sketch, "E40", {"start": v(-31.07, -83.3) * mm, "end": v(-30.1, -80.95) * mm});
            skSolve(sketch);
        }
        {
            var Q0;
            Q0 = qSketchRegion(id + "F6", true);
            var Q1;
            {var subQ0=sQuery(id+"F1.wireOp",EDGE,"E21.0");var subQ1=sQuery(id+"F1.wireOp",EDGE,"E20.0");var subQ2=sQuery(id+"F1.wireOp",EDGE,"E19.0");var subQ3=sQuery(id+"F1.wireOp",EDGE,"E18.0");var subQ4=sQuery(id+"F1.wireOp",EDGE,"E17.0");var subQ5=sQuery(id+"F1.wireOp",EDGE,"E16.0");var subQ6=sQuery(id+"F1.wireOp",EDGE,"E15.0");var subQ7=sQuery(id+"F1.wireOp",EDGE,"E14.0");var subQ8=sQuery(id+"F1.wireOp",EDGE,"E13.0");Q1=makeQuery(id+"F4.boolean.opBoolean","MERGE",FACE,{"derivedFrom":[makeQuery(id+"F2.opExtrude","CAP_FACE",FACE,{"disambiguationData":[OSD([subQ8,subQ7,subQ6,subQ5,subQ4,subQ3,subQ2,subQ1,subQ0])],"isStart":true}),makeQuery(id+"F4.opExtrude","CAP_FACE",FACE,{"disambiguationData":[OSD([subQ8,subQ7,subQ6,subQ5,subQ4,subQ3,subQ2,subQ1,subQ0]),ownerDisambiguation([makeQuery(id+"F4.opExtrude","SWEPT_BODY",BODY,{"disambiguationData":[OSD([sQuery(id+"F3.wireOp",EDGE,"E22"),sQuery(id+"F3.wireOp",EDGE,"E23.0"),sQuery(id+"F3.wireOp",EDGE,"E25"),sQuery(id+"F3.wireOp",EDGE,"E26.MirrorCS")])]})])],"isStart":true}),makeQuery(id+"F4.opExtrude","CAP_FACE",FACE,{"disambiguationData":[OSD([subQ8,subQ7,subQ6,subQ5,subQ4,subQ3,subQ2,subQ1,subQ0]),ownerDisambiguation([makeQuery(id+"F4.opExtrude","SWEPT_BODY",BODY,{"disambiguationData":[OSD([sQuery(id+"F3.wireOp",EDGE,"E27.1.0"),sQuery(id+"F3.wireOp",EDGE,"E27.1.1"),sQuery(id+"F3.wireOp",EDGE,"E27.1.2"),sQuery(id+"F3.wireOp",EDGE,"E27.1.3")])]})])],"isStart":true}),makeQuery(id+"F4.opExtrude","CAP_FACE",FACE,{"disambiguationData":[OSD([subQ8,subQ7,subQ6,subQ5,subQ4,subQ3,subQ2,subQ1,subQ0]),ownerDisambiguation([makeQuery(id+"F4.opExtrude","SWEPT_BODY",BODY,{"disambiguationData":[OSD([sQuery(id+"F3.wireOp",EDGE,"E27.2.0"),sQuery(id+"F3.wireOp",EDGE,"E27.2.1"),sQuery(id+"F3.wireOp",EDGE,"E27.2.2"),sQuery(id+"F3.wireOp",EDGE,"E27.2.3")])]})])],"isStart":true}),makeQuery(id+"F4.opExtrude","CAP_FACE",FACE,{"disambiguationData":[OSD([subQ8,subQ7,subQ6,subQ5,subQ4,subQ3,subQ2,subQ1,subQ0]),ownerDisambiguation([makeQuery(id+"F4.opExtrude","SWEPT_BODY",BODY,{"disambiguationData":[OSD([sQuery(id+"F3.wireOp",EDGE,"E27.3.0"),sQuery(id+"F3.wireOp",EDGE,"E27.3.1"),sQuery(id+"F3.wireOp",EDGE,"E27.3.2"),sQuery(id+"F3.wireOp",EDGE,"E27.3.3")])]})])],"isStart":true}),makeQuery(id+"F4.opExtrude","CAP_FACE",FACE,{"disambiguationData":[OSD([subQ8,subQ7,subQ6,subQ5,subQ4,subQ3,subQ2,subQ1,subQ0]),ownerDisambiguation([makeQuery(id+"F4.opExtrude","SWEPT_BODY",BODY,{"disambiguationData":[OSD([sQuery(id+"F3.wireOp",EDGE,"E27.4.0"),sQuery(id+"F3.wireOp",EDGE,"E27.4.1"),sQuery(id+"F3.wireOp",EDGE,"E27.4.2"),sQuery(id+"F3.wireOp",EDGE,"E27.4.3")])]})])],"isStart":true}),makeQuery(id+"F4.opExtrude","CAP_FACE",FACE,{"disambiguationData":[OSD([subQ8,subQ7,subQ6,subQ5,subQ4,subQ3,subQ2,subQ1,subQ0]),ownerDisambiguation([makeQuery(id+"F4.opExtrude","SWEPT_BODY",BODY,{"disambiguationData":[OSD([sQuery(id+"F3.wireOp",EDGE,"E27.5.0"),sQuery(id+"F3.wireOp",EDGE,"E27.5.1"),sQuery(id+"F3.wireOp",EDGE,"E27.5.2"),sQuery(id+"F3.wireOp",EDGE,"E27.5.3")])]})])],"isStart":true}),makeQuery(id+"F4.opExtrude","CAP_FACE",FACE,{"disambiguationData":[OSD([subQ8,subQ7,subQ6,subQ5,subQ4,subQ3,subQ2,subQ1,subQ0]),ownerDisambiguation([makeQuery(id+"F4.opExtrude","SWEPT_BODY",BODY,{"disambiguationData":[OSD([sQuery(id+"F3.wireOp",EDGE,"E27.6.0"),sQuery(id+"F3.wireOp",EDGE,"E27.6.1"),sQuery(id+"F3.wireOp",EDGE,"E27.6.2"),sQuery(id+"F3.wireOp",EDGE,"E27.6.3")])]})])],"isStart":true}),makeQuery(id+"F4.opExtrude","CAP_FACE",FACE,{"disambiguationData":[OSD([subQ8,subQ7,subQ6,subQ5,subQ4,subQ3,subQ2,subQ1,subQ0]),ownerDisambiguation([makeQuery(id+"F4.opExtrude","SWEPT_BODY",BODY,{"disambiguationData":[OSD([sQuery(id+"F3.wireOp",EDGE,"E27.7.0"),sQuery(id+"F3.wireOp",EDGE,"E27.7.1"),sQuery(id+"F3.wireOp",EDGE,"E27.7.2"),sQuery(id+"F3.wireOp",EDGE,"E27.7.3")])]})])],"isStart":true}),makeQuery(id+"F4.opExtrude","CAP_FACE",FACE,{"disambiguationData":[OSD([subQ8,subQ7,subQ6,subQ5,subQ4,subQ3,subQ2,subQ1,subQ0]),ownerDisambiguation([makeQuery(id+"F4.opExtrude","SWEPT_BODY",BODY,{"disambiguationData":[OSD([sQuery(id+"F3.wireOp",EDGE,"E27.8.0"),sQuery(id+"F3.wireOp",EDGE,"E27.8.1"),sQuery(id+"F3.wireOp",EDGE,"E27.8.2"),sQuery(id+"F3.wireOp",EDGE,"E27.8.3")])]})])],"isStart":true}),makeQuery(id+"F4.opExtrude","CAP_FACE",FACE,{"disambiguationData":[OSD([subQ8,subQ7,subQ6,subQ5,subQ4,subQ3,subQ2,subQ1,subQ0]),ownerDisambiguation([makeQuery(id+"F4.opExtrude","SWEPT_BODY",BODY,{"disambiguationData":[OSD([sQuery(id+"F3.wireOp",EDGE,"E27.9.0"),sQuery(id+"F3.wireOp",EDGE,"E27.9.1"),sQuery(id+"F3.wireOp",EDGE,"E27.9.2"),sQuery(id+"F3.wireOp",EDGE,"E27.9.3")])]})])],"isStart":true}),makeQuery(id+"F4.opExtrude","CAP_FACE",FACE,{"disambiguationData":[OSD([subQ8,subQ7,subQ6,subQ5,subQ4,subQ3,subQ2,subQ1,subQ0]),ownerDisambiguation([makeQuery(id+"F4.opExtrude","SWEPT_BODY",BODY,{"disambiguationData":[OSD([sQuery(id+"F3.wireOp",EDGE,"E27.10.0"),sQuery(id+"F3.wireOp",EDGE,"E27.10.1"),sQuery(id+"F3.wireOp",EDGE,"E27.10.2"),sQuery(id+"F3.wireOp",EDGE,"E27.10.3")])]})])],"isStart":true}),makeQuery(id+"F4.opExtrude","CAP_FACE",FACE,{"disambiguationData":[OSD([subQ8,subQ7,subQ6,subQ5,subQ4,subQ3,subQ2,subQ1,subQ0]),ownerDisambiguation([makeQuery(id+"F4.opExtrude","SWEPT_BODY",BODY,{"disambiguationData":[OSD([sQuery(id+"F3.wireOp",EDGE,"E27.11.0"),sQuery(id+"F3.wireOp",EDGE,"E27.11.1"),sQuery(id+"F3.wireOp",EDGE,"E27.11.2"),sQuery(id+"F3.wireOp",EDGE,"E27.11.3")])]})])],"isStart":true}),makeQuery(id+"F4.opExtrude","CAP_FACE",FACE,{"disambiguationData":[OSD([subQ8,subQ7,subQ6,subQ5,subQ4,subQ3,subQ2,subQ1,subQ0]),ownerDisambiguation([makeQuery(id+"F4.opExtrude","SWEPT_BODY",BODY,{"disambiguationData":[OSD([sQuery(id+"F3.wireOp",EDGE,"E27.12.0"),sQuery(id+"F3.wireOp",EDGE,"E27.12.1"),sQuery(id+"F3.wireOp",EDGE,"E27.12.2"),sQuery(id+"F3.wireOp",EDGE,"E27.12.3")])]})])],"isStart":true}),makeQuery(id+"F4.opExtrude","CAP_FACE",FACE,{"disambiguationData":[OSD([subQ8,subQ7,subQ6,subQ5,subQ4,subQ3,subQ2,subQ1,subQ0]),ownerDisambiguation([makeQuery(id+"F4.opExtrude","SWEPT_BODY",BODY,{"disambiguationData":[OSD([sQuery(id+"F3.wireOp",EDGE,"E27.13.0"),sQuery(id+"F3.wireOp",EDGE,"E27.13.1"),sQuery(id+"F3.wireOp",EDGE,"E27.13.2"),sQuery(id+"F3.wireOp",EDGE,"E27.13.3")])]})])],"isStart":true}),makeQuery(id+"F4.opExtrude","CAP_FACE",FACE,{"disambiguationData":[OSD([subQ8,subQ7,subQ6,subQ5,subQ4,subQ3,subQ2,subQ1,subQ0]),ownerDisambiguation([makeQuery(id+"F4.opExtrude","SWEPT_BODY",BODY,{"disambiguationData":[OSD([sQuery(id+"F3.wireOp",EDGE,"E27.14.0"),sQuery(id+"F3.wireOp",EDGE,"E27.14.1"),sQuery(id+"F3.wireOp",EDGE,"E27.14.2"),sQuery(id+"F3.wireOp",EDGE,"E27.14.3")])]})])],"isStart":true}),makeQuery(id+"F4.opExtrude","CAP_FACE",FACE,{"disambiguationData":[OSD([subQ8,subQ7,subQ6,subQ5,subQ4,subQ3,subQ2,subQ1,subQ0]),ownerDisambiguation([makeQuery(id+"F4.opExtrude","SWEPT_BODY",BODY,{"disambiguationData":[OSD([sQuery(id+"F3.wireOp",EDGE,"E27.15.0"),sQuery(id+"F3.wireOp",EDGE,"E27.15.1"),sQuery(id+"F3.wireOp",EDGE,"E27.15.2"),sQuery(id+"F3.wireOp",EDGE,"E27.15.3")])]})])],"isStart":true}),makeQuery(id+"F4.opExtrude","CAP_FACE",FACE,{"disambiguationData":[OSD([subQ8,subQ7,subQ6,subQ5,subQ4,subQ3,subQ2,subQ1,subQ0]),ownerDisambiguation([makeQuery(id+"F4.opExtrude","SWEPT_BODY",BODY,{"disambiguationData":[OSD([sQuery(id+"F3.wireOp",EDGE,"E27.16.0"),sQuery(id+"F3.wireOp",EDGE,"E27.16.1"),sQuery(id+"F3.wireOp",EDGE,"E27.16.2"),sQuery(id+"F3.wireOp",EDGE,"E27.16.3")])]})])],"isStart":true}),makeQuery(id+"F4.opExtrude","CAP_FACE",FACE,{"disambiguationData":[OSD([subQ8,subQ7,subQ6,subQ5,subQ4,subQ3,subQ2,subQ1,subQ0]),ownerDisambiguation([makeQuery(id+"F4.opExtrude","SWEPT_BODY",BODY,{"disambiguationData":[OSD([sQuery(id+"F3.wireOp",EDGE,"E27.17.0"),sQuery(id+"F3.wireOp",EDGE,"E27.17.1"),sQuery(id+"F3.wireOp",EDGE,"E27.17.2"),sQuery(id+"F3.wireOp",EDGE,"E27.17.3")])]})])],"isStart":true}),makeQuery(id+"F4.opExtrude","CAP_FACE",FACE,{"disambiguationData":[OSD([subQ8,subQ7,subQ6,subQ5,subQ4,subQ3,subQ2,subQ1,subQ0]),ownerDisambiguation([makeQuery(id+"F4.opExtrude","SWEPT_BODY",BODY,{"disambiguationData":[OSD([sQuery(id+"F3.wireOp",EDGE,"E27.18.0"),sQuery(id+"F3.wireOp",EDGE,"E27.18.1"),sQuery(id+"F3.wireOp",EDGE,"E27.18.2"),sQuery(id+"F3.wireOp",EDGE,"E27.18.3")])]})])],"isStart":true}),makeQuery(id+"F4.opExtrude","CAP_FACE",FACE,{"disambiguationData":[OSD([subQ8,subQ7,subQ6,subQ5,subQ4,subQ3,subQ2,subQ1,subQ0]),ownerDisambiguation([makeQuery(id+"F4.opExtrude","SWEPT_BODY",BODY,{"disambiguationData":[OSD([sQuery(id+"F3.wireOp",EDGE,"E27.19.0"),sQuery(id+"F3.wireOp",EDGE,"E27.19.1"),sQuery(id+"F3.wireOp",EDGE,"E27.19.2"),sQuery(id+"F3.wireOp",EDGE,"E27.19.3")])]})])],"isStart":true}),makeQuery(id+"F4.opExtrude","CAP_FACE",FACE,{"disambiguationData":[OSD([subQ8,subQ7,subQ6,subQ5,subQ4,subQ3,subQ2,subQ1,subQ0]),ownerDisambiguation([makeQuery(id+"F4.opExtrude","SWEPT_BODY",BODY,{"disambiguationData":[OSD([sQuery(id+"F3.wireOp",EDGE,"E27.20.0"),sQuery(id+"F3.wireOp",EDGE,"E27.20.1"),sQuery(id+"F3.wireOp",EDGE,"E27.20.2"),sQuery(id+"F3.wireOp",EDGE,"E27.20.3")])]})])],"isStart":true}),makeQuery(id+"F4.opExtrude","CAP_FACE",FACE,{"disambiguationData":[OSD([subQ8,subQ7,subQ6,subQ5,subQ4,subQ3,subQ2,subQ1,subQ0]),ownerDisambiguation([makeQuery(id+"F4.opExtrude","SWEPT_BODY",BODY,{"disambiguationData":[OSD([sQuery(id+"F3.wireOp",EDGE,"E27.21.0"),sQuery(id+"F3.wireOp",EDGE,"E27.21.1"),sQuery(id+"F3.wireOp",EDGE,"E27.21.2"),sQuery(id+"F3.wireOp",EDGE,"E27.21.3")])]})])],"isStart":true}),makeQuery(id+"F4.opExtrude","CAP_FACE",FACE,{"disambiguationData":[OSD([subQ8,subQ7,subQ6,subQ5,subQ4,subQ3,subQ2,subQ1,subQ0]),ownerDisambiguation([makeQuery(id+"F4.opExtrude","SWEPT_BODY",BODY,{"disambiguationData":[OSD([sQuery(id+"F3.wireOp",EDGE,"E27.22.0"),sQuery(id+"F3.wireOp",EDGE,"E27.22.1"),sQuery(id+"F3.wireOp",EDGE,"E27.22.2"),sQuery(id+"F3.wireOp",EDGE,"E27.22.3")])]})])],"isStart":true}),makeQuery(id+"F4.opExtrude","CAP_FACE",FACE,{"disambiguationData":[OSD([subQ8,subQ7,subQ6,subQ5,subQ4,subQ3,subQ2,subQ1,subQ0]),ownerDisambiguation([makeQuery(id+"F4.opExtrude","SWEPT_BODY",BODY,{"disambiguationData":[OSD([sQuery(id+"F3.wireOp",EDGE,"E27.23.0"),sQuery(id+"F3.wireOp",EDGE,"E27.23.1"),sQuery(id+"F3.wireOp",EDGE,"E27.23.2"),sQuery(id+"F3.wireOp",EDGE,"E27.23.3")])]})])],"isStart":true}),makeQuery(id+"F4.opExtrude","CAP_FACE",FACE,{"disambiguationData":[OSD([subQ8,subQ7,subQ6,subQ5,subQ4,subQ3,subQ2,subQ1,subQ0]),ownerDisambiguation([makeQuery(id+"F4.opExtrude","SWEPT_BODY",BODY,{"disambiguationData":[OSD([sQuery(id+"F3.wireOp",EDGE,"E27.24.0"),sQuery(id+"F3.wireOp",EDGE,"E27.24.1"),sQuery(id+"F3.wireOp",EDGE,"E27.24.2"),sQuery(id+"F3.wireOp",EDGE,"E27.24.3")])]})])],"isStart":true}),makeQuery(id+"F4.opExtrude","CAP_FACE",FACE,{"disambiguationData":[OSD([subQ8,subQ7,subQ6,subQ5,subQ4,subQ3,subQ2,subQ1,subQ0]),ownerDisambiguation([makeQuery(id+"F4.opExtrude","SWEPT_BODY",BODY,{"disambiguationData":[OSD([sQuery(id+"F3.wireOp",EDGE,"E27.25.0"),sQuery(id+"F3.wireOp",EDGE,"E27.25.1"),sQuery(id+"F3.wireOp",EDGE,"E27.25.2"),sQuery(id+"F3.wireOp",EDGE,"E27.25.3")])]})])],"isStart":true}),makeQuery(id+"F4.opExtrude","CAP_FACE",FACE,{"disambiguationData":[OSD([subQ8,subQ7,subQ6,subQ5,subQ4,subQ3,subQ2,subQ1,subQ0]),ownerDisambiguation([makeQuery(id+"F4.opExtrude","SWEPT_BODY",BODY,{"disambiguationData":[OSD([sQuery(id+"F3.wireOp",EDGE,"E27.26.0"),sQuery(id+"F3.wireOp",EDGE,"E27.26.1"),sQuery(id+"F3.wireOp",EDGE,"E27.26.2"),sQuery(id+"F3.wireOp",EDGE,"E27.26.3")])]})])],"isStart":true}),makeQuery(id+"F4.opExtrude","CAP_FACE",FACE,{"disambiguationData":[OSD([subQ8,subQ7,subQ6,subQ5,subQ4,subQ3,subQ2,subQ1,subQ0]),ownerDisambiguation([makeQuery(id+"F4.opExtrude","SWEPT_BODY",BODY,{"disambiguationData":[OSD([sQuery(id+"F3.wireOp",EDGE,"E27.27.0"),sQuery(id+"F3.wireOp",EDGE,"E27.27.1"),sQuery(id+"F3.wireOp",EDGE,"E27.27.2"),sQuery(id+"F3.wireOp",EDGE,"E27.27.3")])]})])],"isStart":true}),makeQuery(id+"F4.opExtrude","CAP_FACE",FACE,{"disambiguationData":[OSD([subQ8,subQ7,subQ6,subQ5,subQ4,subQ3,subQ2,subQ1,subQ0]),ownerDisambiguation([makeQuery(id+"F4.opExtrude","SWEPT_BODY",BODY,{"disambiguationData":[OSD([sQuery(id+"F3.wireOp",EDGE,"E27.28.0"),sQuery(id+"F3.wireOp",EDGE,"E27.28.1"),sQuery(id+"F3.wireOp",EDGE,"E27.28.2"),sQuery(id+"F3.wireOp",EDGE,"E27.28.3")])]})])],"isStart":true}),makeQuery(id+"F4.opExtrude","CAP_FACE",FACE,{"disambiguationData":[OSD([subQ8,subQ7,subQ6,subQ5,subQ4,subQ3,subQ2,subQ1,subQ0]),ownerDisambiguation([makeQuery(id+"F4.opExtrude","SWEPT_BODY",BODY,{"disambiguationData":[OSD([sQuery(id+"F3.wireOp",EDGE,"E27.29.0"),sQuery(id+"F3.wireOp",EDGE,"E27.29.1"),sQuery(id+"F3.wireOp",EDGE,"E27.29.2"),sQuery(id+"F3.wireOp",EDGE,"E27.29.3")])]})])],"isStart":true}),makeQuery(id+"F4.opExtrude","CAP_FACE",FACE,{"disambiguationData":[OSD([subQ8,subQ7,subQ6,subQ5,subQ4,subQ3,subQ2,subQ1,subQ0]),ownerDisambiguation([makeQuery(id+"F4.opExtrude","SWEPT_BODY",BODY,{"disambiguationData":[OSD([sQuery(id+"F3.wireOp",EDGE,"E27.30.0"),sQuery(id+"F3.wireOp",EDGE,"E27.30.1"),sQuery(id+"F3.wireOp",EDGE,"E27.30.2"),sQuery(id+"F3.wireOp",EDGE,"E27.30.3")])]})])],"isStart":true}),makeQuery(id+"F4.opExtrude","CAP_FACE",FACE,{"disambiguationData":[OSD([subQ8,subQ7,subQ6,subQ5,subQ4,subQ3,subQ2,subQ1,subQ0]),ownerDisambiguation([makeQuery(id+"F4.opExtrude","SWEPT_BODY",BODY,{"disambiguationData":[OSD([sQuery(id+"F3.wireOp",EDGE,"E27.31.0"),sQuery(id+"F3.wireOp",EDGE,"E27.31.1"),sQuery(id+"F3.wireOp",EDGE,"E27.31.2"),sQuery(id+"F3.wireOp",EDGE,"E27.31.3")])]})])],"isStart":true}),makeQuery(id+"F4.opExtrude","CAP_FACE",FACE,{"disambiguationData":[OSD([subQ8,subQ7,subQ6,subQ5,subQ4,subQ3,subQ2,subQ1,subQ0]),ownerDisambiguation([makeQuery(id+"F4.opExtrude","SWEPT_BODY",BODY,{"disambiguationData":[OSD([sQuery(id+"F3.wireOp",EDGE,"E27.32.0"),sQuery(id+"F3.wireOp",EDGE,"E27.32.1"),sQuery(id+"F3.wireOp",EDGE,"E27.32.2"),sQuery(id+"F3.wireOp",EDGE,"E27.32.3")])]})])],"isStart":true}),makeQuery(id+"F4.opExtrude","CAP_FACE",FACE,{"disambiguationData":[OSD([subQ8,subQ7,subQ6,subQ5,subQ4,subQ3,subQ2,subQ1,subQ0]),ownerDisambiguation([makeQuery(id+"F4.opExtrude","SWEPT_BODY",BODY,{"disambiguationData":[OSD([sQuery(id+"F3.wireOp",EDGE,"E27.33.0"),sQuery(id+"F3.wireOp",EDGE,"E27.33.1"),sQuery(id+"F3.wireOp",EDGE,"E27.33.2"),sQuery(id+"F3.wireOp",EDGE,"E27.33.3")])]})])],"isStart":true}),makeQuery(id+"F4.opExtrude","CAP_FACE",FACE,{"disambiguationData":[OSD([subQ8,subQ7,subQ6,subQ5,subQ4,subQ3,subQ2,subQ1,subQ0]),ownerDisambiguation([makeQuery(id+"F4.opExtrude","SWEPT_BODY",BODY,{"disambiguationData":[OSD([sQuery(id+"F3.wireOp",EDGE,"E27.34.0"),sQuery(id+"F3.wireOp",EDGE,"E27.34.1"),sQuery(id+"F3.wireOp",EDGE,"E27.34.2"),sQuery(id+"F3.wireOp",EDGE,"E27.34.3")])]})])],"isStart":true}),makeQuery(id+"F4.opExtrude","CAP_FACE",FACE,{"disambiguationData":[OSD([subQ8,subQ7,subQ6,subQ5,subQ4,subQ3,subQ2,subQ1,subQ0]),ownerDisambiguation([makeQuery(id+"F4.opExtrude","SWEPT_BODY",BODY,{"disambiguationData":[OSD([sQuery(id+"F3.wireOp",EDGE,"E27.35.0"),sQuery(id+"F3.wireOp",EDGE,"E27.35.1"),sQuery(id+"F3.wireOp",EDGE,"E27.35.2"),sQuery(id+"F3.wireOp",EDGE,"E27.35.3")])]})])],"isStart":true}),makeQuery(id+"F4.opExtrude","CAP_FACE",FACE,{"disambiguationData":[OSD([subQ8,subQ7,subQ6,subQ5,subQ4,subQ3,subQ2,subQ1,subQ0]),ownerDisambiguation([makeQuery(id+"F4.opExtrude","SWEPT_BODY",BODY,{"disambiguationData":[OSD([sQuery(id+"F3.wireOp",EDGE,"E27.36.0"),sQuery(id+"F3.wireOp",EDGE,"E27.36.1"),sQuery(id+"F3.wireOp",EDGE,"E27.36.2"),sQuery(id+"F3.wireOp",EDGE,"E27.36.3")])]})])],"isStart":true}),makeQuery(id+"F4.opExtrude","CAP_FACE",FACE,{"disambiguationData":[OSD([subQ8,subQ7,subQ6,subQ5,subQ4,subQ3,subQ2,subQ1,subQ0]),ownerDisambiguation([makeQuery(id+"F4.opExtrude","SWEPT_BODY",BODY,{"disambiguationData":[OSD([sQuery(id+"F3.wireOp",EDGE,"E27.37.0"),sQuery(id+"F3.wireOp",EDGE,"E27.37.1"),sQuery(id+"F3.wireOp",EDGE,"E27.37.2"),sQuery(id+"F3.wireOp",EDGE,"E27.37.3")])]})])],"isStart":true}),makeQuery(id+"F4.opExtrude","CAP_FACE",FACE,{"disambiguationData":[OSD([subQ8,subQ7,subQ6,subQ5,subQ4,subQ3,subQ2,subQ1,subQ0]),ownerDisambiguation([makeQuery(id+"F4.opExtrude","SWEPT_BODY",BODY,{"disambiguationData":[OSD([sQuery(id+"F3.wireOp",EDGE,"E27.38.0"),sQuery(id+"F3.wireOp",EDGE,"E27.38.1"),sQuery(id+"F3.wireOp",EDGE,"E27.38.2"),sQuery(id+"F3.wireOp",EDGE,"E27.38.3")])]})])],"isStart":true}),makeQuery(id+"F4.opExtrude","CAP_FACE",FACE,{"disambiguationData":[OSD([subQ8,subQ7,subQ6,subQ5,subQ4,subQ3,subQ2,subQ1,subQ0]),ownerDisambiguation([makeQuery(id+"F4.opExtrude","SWEPT_BODY",BODY,{"disambiguationData":[OSD([sQuery(id+"F3.wireOp",EDGE,"E27.39.0"),sQuery(id+"F3.wireOp",EDGE,"E27.39.1"),sQuery(id+"F3.wireOp",EDGE,"E27.39.2"),sQuery(id+"F3.wireOp",EDGE,"E27.39.3")])]})])],"isStart":true}),makeQuery(id+"F4.opExtrude","CAP_FACE",FACE,{"disambiguationData":[OSD([subQ8,subQ7,subQ6,subQ5,subQ4,subQ3,subQ2,subQ1,subQ0]),ownerDisambiguation([makeQuery(id+"F4.opExtrude","SWEPT_BODY",BODY,{"disambiguationData":[OSD([sQuery(id+"F3.wireOp",EDGE,"E27.40.0"),sQuery(id+"F3.wireOp",EDGE,"E27.40.1"),sQuery(id+"F3.wireOp",EDGE,"E27.40.2"),sQuery(id+"F3.wireOp",EDGE,"E27.40.3")])]})])],"isStart":true}),makeQuery(id+"F4.opExtrude","CAP_FACE",FACE,{"disambiguationData":[OSD([subQ8,subQ7,subQ6,subQ5,subQ4,subQ3,subQ2,subQ1,subQ0]),ownerDisambiguation([makeQuery(id+"F4.opExtrude","SWEPT_BODY",BODY,{"disambiguationData":[OSD([sQuery(id+"F3.wireOp",EDGE,"E27.41.0"),sQuery(id+"F3.wireOp",EDGE,"E27.41.1"),sQuery(id+"F3.wireOp",EDGE,"E27.41.2"),sQuery(id+"F3.wireOp",EDGE,"E27.41.3")])]})])],"isStart":true}),makeQuery(id+"F4.opExtrude","CAP_FACE",FACE,{"disambiguationData":[OSD([subQ8,subQ7,subQ6,subQ5,subQ4,subQ3,subQ2,subQ1,subQ0]),ownerDisambiguation([makeQuery(id+"F4.opExtrude","SWEPT_BODY",BODY,{"disambiguationData":[OSD([sQuery(id+"F3.wireOp",EDGE,"E27.42.0"),sQuery(id+"F3.wireOp",EDGE,"E27.42.1"),sQuery(id+"F3.wireOp",EDGE,"E27.42.2"),sQuery(id+"F3.wireOp",EDGE,"E27.42.3")])]})])],"isStart":true}),makeQuery(id+"F4.opExtrude","CAP_FACE",FACE,{"disambiguationData":[OSD([subQ8,subQ7,subQ6,subQ5,subQ4,subQ3,subQ2,subQ1,subQ0]),ownerDisambiguation([makeQuery(id+"F4.opExtrude","SWEPT_BODY",BODY,{"disambiguationData":[OSD([sQuery(id+"F3.wireOp",EDGE,"E27.43.0"),sQuery(id+"F3.wireOp",EDGE,"E27.43.1"),sQuery(id+"F3.wireOp",EDGE,"E27.43.2"),sQuery(id+"F3.wireOp",EDGE,"E27.43.3")])]})])],"isStart":true}),makeQuery(id+"F4.opExtrude","CAP_FACE",FACE,{"disambiguationData":[OSD([subQ8,subQ7,subQ6,subQ5,subQ4,subQ3,subQ2,subQ1,subQ0]),ownerDisambiguation([makeQuery(id+"F4.opExtrude","SWEPT_BODY",BODY,{"disambiguationData":[OSD([sQuery(id+"F3.wireOp",EDGE,"E27.44.0"),sQuery(id+"F3.wireOp",EDGE,"E27.44.1"),sQuery(id+"F3.wireOp",EDGE,"E27.44.2"),sQuery(id+"F3.wireOp",EDGE,"E27.44.3")])]})])],"isStart":true}),makeQuery(id+"F4.opExtrude","CAP_FACE",FACE,{"disambiguationData":[OSD([subQ8,subQ7,subQ6,subQ5,subQ4,subQ3,subQ2,subQ1,subQ0]),ownerDisambiguation([makeQuery(id+"F4.opExtrude","SWEPT_BODY",BODY,{"disambiguationData":[OSD([sQuery(id+"F3.wireOp",EDGE,"E27.45.0"),sQuery(id+"F3.wireOp",EDGE,"E27.45.1"),sQuery(id+"F3.wireOp",EDGE,"E27.45.2"),sQuery(id+"F3.wireOp",EDGE,"E27.45.3")])]})])],"isStart":true}),makeQuery(id+"F4.opExtrude","CAP_FACE",FACE,{"disambiguationData":[OSD([subQ8,subQ7,subQ6,subQ5,subQ4,subQ3,subQ2,subQ1,subQ0]),ownerDisambiguation([makeQuery(id+"F4.opExtrude","SWEPT_BODY",BODY,{"disambiguationData":[OSD([sQuery(id+"F3.wireOp",EDGE,"E27.46.0"),sQuery(id+"F3.wireOp",EDGE,"E27.46.1"),sQuery(id+"F3.wireOp",EDGE,"E27.46.2"),sQuery(id+"F3.wireOp",EDGE,"E27.46.3")])]})])],"isStart":true}),makeQuery(id+"F4.opExtrude","CAP_FACE",FACE,{"disambiguationData":[OSD([subQ8,subQ7,subQ6,subQ5,subQ4,subQ3,subQ2,subQ1,subQ0]),ownerDisambiguation([makeQuery(id+"F4.opExtrude","SWEPT_BODY",BODY,{"disambiguationData":[OSD([sQuery(id+"F3.wireOp",EDGE,"E27.47.0"),sQuery(id+"F3.wireOp",EDGE,"E27.47.1"),sQuery(id+"F3.wireOp",EDGE,"E27.47.2"),sQuery(id+"F3.wireOp",EDGE,"E27.47.3")])]})])],"isStart":true})]});}
            var Q2;
            {var subQ0=sQuery(id+"F1.wireOp",EDGE,"E21.0");var subQ1=sQuery(id+"F1.wireOp",EDGE,"E20.0");var subQ2=sQuery(id+"F1.wireOp",EDGE,"E19.0");var subQ3=sQuery(id+"F1.wireOp",EDGE,"E18.0");var subQ4=sQuery(id+"F1.wireOp",EDGE,"E17.0");var subQ5=sQuery(id+"F1.wireOp",EDGE,"E16.0");var subQ6=sQuery(id+"F1.wireOp",EDGE,"E15.0");var subQ7=sQuery(id+"F1.wireOp",EDGE,"E14.0");var subQ8=sQuery(id+"F1.wireOp",EDGE,"E13.0");Q2=makeQuery(id+"F4.boolean.opBoolean","MERGE",FACE,{"derivedFrom":[makeQuery(id+"F2.opExtrude","CAP_FACE",FACE,{"disambiguationData":[OSD([subQ8,subQ7,subQ6,subQ5,subQ4,subQ3,subQ2,subQ1,subQ0])],"isStart":false}),makeQuery(id+"F4.opExtrude","CAP_FACE",FACE,{"disambiguationData":[OSD([subQ8,subQ7,subQ6,subQ5,subQ4,subQ3,subQ2,subQ1,subQ0]),ownerDisambiguation([makeQuery(id+"F4.opExtrude","SWEPT_BODY",BODY,{"disambiguationData":[OSD([sQuery(id+"F3.wireOp",EDGE,"E22"),sQuery(id+"F3.wireOp",EDGE,"E23.0"),sQuery(id+"F3.wireOp",EDGE,"E25"),sQuery(id+"F3.wireOp",EDGE,"E26.MirrorCS")])]})])],"isStart":false}),makeQuery(id+"F4.opExtrude","CAP_FACE",FACE,{"disambiguationData":[OSD([subQ8,subQ7,subQ6,subQ5,subQ4,subQ3,subQ2,subQ1,subQ0]),ownerDisambiguation([makeQuery(id+"F4.opExtrude","SWEPT_BODY",BODY,{"disambiguationData":[OSD([sQuery(id+"F3.wireOp",EDGE,"E27.1.0"),sQuery(id+"F3.wireOp",EDGE,"E27.1.1"),sQuery(id+"F3.wireOp",EDGE,"E27.1.2"),sQuery(id+"F3.wireOp",EDGE,"E27.1.3")])]})])],"isStart":false}),makeQuery(id+"F4.opExtrude","CAP_FACE",FACE,{"disambiguationData":[OSD([subQ8,subQ7,subQ6,subQ5,subQ4,subQ3,subQ2,subQ1,subQ0]),ownerDisambiguation([makeQuery(id+"F4.opExtrude","SWEPT_BODY",BODY,{"disambiguationData":[OSD([sQuery(id+"F3.wireOp",EDGE,"E27.2.0"),sQuery(id+"F3.wireOp",EDGE,"E27.2.1"),sQuery(id+"F3.wireOp",EDGE,"E27.2.2"),sQuery(id+"F3.wireOp",EDGE,"E27.2.3")])]})])],"isStart":false}),makeQuery(id+"F4.opExtrude","CAP_FACE",FACE,{"disambiguationData":[OSD([subQ8,subQ7,subQ6,subQ5,subQ4,subQ3,subQ2,subQ1,subQ0]),ownerDisambiguation([makeQuery(id+"F4.opExtrude","SWEPT_BODY",BODY,{"disambiguationData":[OSD([sQuery(id+"F3.wireOp",EDGE,"E27.3.0"),sQuery(id+"F3.wireOp",EDGE,"E27.3.1"),sQuery(id+"F3.wireOp",EDGE,"E27.3.2"),sQuery(id+"F3.wireOp",EDGE,"E27.3.3")])]})])],"isStart":false}),makeQuery(id+"F4.opExtrude","CAP_FACE",FACE,{"disambiguationData":[OSD([subQ8,subQ7,subQ6,subQ5,subQ4,subQ3,subQ2,subQ1,subQ0]),ownerDisambiguation([makeQuery(id+"F4.opExtrude","SWEPT_BODY",BODY,{"disambiguationData":[OSD([sQuery(id+"F3.wireOp",EDGE,"E27.4.0"),sQuery(id+"F3.wireOp",EDGE,"E27.4.1"),sQuery(id+"F3.wireOp",EDGE,"E27.4.2"),sQuery(id+"F3.wireOp",EDGE,"E27.4.3")])]})])],"isStart":false}),makeQuery(id+"F4.opExtrude","CAP_FACE",FACE,{"disambiguationData":[OSD([subQ8,subQ7,subQ6,subQ5,subQ4,subQ3,subQ2,subQ1,subQ0]),ownerDisambiguation([makeQuery(id+"F4.opExtrude","SWEPT_BODY",BODY,{"disambiguationData":[OSD([sQuery(id+"F3.wireOp",EDGE,"E27.5.0"),sQuery(id+"F3.wireOp",EDGE,"E27.5.1"),sQuery(id+"F3.wireOp",EDGE,"E27.5.2"),sQuery(id+"F3.wireOp",EDGE,"E27.5.3")])]})])],"isStart":false}),makeQuery(id+"F4.opExtrude","CAP_FACE",FACE,{"disambiguationData":[OSD([subQ8,subQ7,subQ6,subQ5,subQ4,subQ3,subQ2,subQ1,subQ0]),ownerDisambiguation([makeQuery(id+"F4.opExtrude","SWEPT_BODY",BODY,{"disambiguationData":[OSD([sQuery(id+"F3.wireOp",EDGE,"E27.6.0"),sQuery(id+"F3.wireOp",EDGE,"E27.6.1"),sQuery(id+"F3.wireOp",EDGE,"E27.6.2"),sQuery(id+"F3.wireOp",EDGE,"E27.6.3")])]})])],"isStart":false}),makeQuery(id+"F4.opExtrude","CAP_FACE",FACE,{"disambiguationData":[OSD([subQ8,subQ7,subQ6,subQ5,subQ4,subQ3,subQ2,subQ1,subQ0]),ownerDisambiguation([makeQuery(id+"F4.opExtrude","SWEPT_BODY",BODY,{"disambiguationData":[OSD([sQuery(id+"F3.wireOp",EDGE,"E27.7.0"),sQuery(id+"F3.wireOp",EDGE,"E27.7.1"),sQuery(id+"F3.wireOp",EDGE,"E27.7.2"),sQuery(id+"F3.wireOp",EDGE,"E27.7.3")])]})])],"isStart":false}),makeQuery(id+"F4.opExtrude","CAP_FACE",FACE,{"disambiguationData":[OSD([subQ8,subQ7,subQ6,subQ5,subQ4,subQ3,subQ2,subQ1,subQ0]),ownerDisambiguation([makeQuery(id+"F4.opExtrude","SWEPT_BODY",BODY,{"disambiguationData":[OSD([sQuery(id+"F3.wireOp",EDGE,"E27.8.0"),sQuery(id+"F3.wireOp",EDGE,"E27.8.1"),sQuery(id+"F3.wireOp",EDGE,"E27.8.2"),sQuery(id+"F3.wireOp",EDGE,"E27.8.3")])]})])],"isStart":false}),makeQuery(id+"F4.opExtrude","CAP_FACE",FACE,{"disambiguationData":[OSD([subQ8,subQ7,subQ6,subQ5,subQ4,subQ3,subQ2,subQ1,subQ0]),ownerDisambiguation([makeQuery(id+"F4.opExtrude","SWEPT_BODY",BODY,{"disambiguationData":[OSD([sQuery(id+"F3.wireOp",EDGE,"E27.9.0"),sQuery(id+"F3.wireOp",EDGE,"E27.9.1"),sQuery(id+"F3.wireOp",EDGE,"E27.9.2"),sQuery(id+"F3.wireOp",EDGE,"E27.9.3")])]})])],"isStart":false}),makeQuery(id+"F4.opExtrude","CAP_FACE",FACE,{"disambiguationData":[OSD([subQ8,subQ7,subQ6,subQ5,subQ4,subQ3,subQ2,subQ1,subQ0]),ownerDisambiguation([makeQuery(id+"F4.opExtrude","SWEPT_BODY",BODY,{"disambiguationData":[OSD([sQuery(id+"F3.wireOp",EDGE,"E27.10.0"),sQuery(id+"F3.wireOp",EDGE,"E27.10.1"),sQuery(id+"F3.wireOp",EDGE,"E27.10.2"),sQuery(id+"F3.wireOp",EDGE,"E27.10.3")])]})])],"isStart":false}),makeQuery(id+"F4.opExtrude","CAP_FACE",FACE,{"disambiguationData":[OSD([subQ8,subQ7,subQ6,subQ5,subQ4,subQ3,subQ2,subQ1,subQ0]),ownerDisambiguation([makeQuery(id+"F4.opExtrude","SWEPT_BODY",BODY,{"disambiguationData":[OSD([sQuery(id+"F3.wireOp",EDGE,"E27.11.0"),sQuery(id+"F3.wireOp",EDGE,"E27.11.1"),sQuery(id+"F3.wireOp",EDGE,"E27.11.2"),sQuery(id+"F3.wireOp",EDGE,"E27.11.3")])]})])],"isStart":false}),makeQuery(id+"F4.opExtrude","CAP_FACE",FACE,{"disambiguationData":[OSD([subQ8,subQ7,subQ6,subQ5,subQ4,subQ3,subQ2,subQ1,subQ0]),ownerDisambiguation([makeQuery(id+"F4.opExtrude","SWEPT_BODY",BODY,{"disambiguationData":[OSD([sQuery(id+"F3.wireOp",EDGE,"E27.12.0"),sQuery(id+"F3.wireOp",EDGE,"E27.12.1"),sQuery(id+"F3.wireOp",EDGE,"E27.12.2"),sQuery(id+"F3.wireOp",EDGE,"E27.12.3")])]})])],"isStart":false}),makeQuery(id+"F4.opExtrude","CAP_FACE",FACE,{"disambiguationData":[OSD([subQ8,subQ7,subQ6,subQ5,subQ4,subQ3,subQ2,subQ1,subQ0]),ownerDisambiguation([makeQuery(id+"F4.opExtrude","SWEPT_BODY",BODY,{"disambiguationData":[OSD([sQuery(id+"F3.wireOp",EDGE,"E27.13.0"),sQuery(id+"F3.wireOp",EDGE,"E27.13.1"),sQuery(id+"F3.wireOp",EDGE,"E27.13.2"),sQuery(id+"F3.wireOp",EDGE,"E27.13.3")])]})])],"isStart":false}),makeQuery(id+"F4.opExtrude","CAP_FACE",FACE,{"disambiguationData":[OSD([subQ8,subQ7,subQ6,subQ5,subQ4,subQ3,subQ2,subQ1,subQ0]),ownerDisambiguation([makeQuery(id+"F4.opExtrude","SWEPT_BODY",BODY,{"disambiguationData":[OSD([sQuery(id+"F3.wireOp",EDGE,"E27.14.0"),sQuery(id+"F3.wireOp",EDGE,"E27.14.1"),sQuery(id+"F3.wireOp",EDGE,"E27.14.2"),sQuery(id+"F3.wireOp",EDGE,"E27.14.3")])]})])],"isStart":false}),makeQuery(id+"F4.opExtrude","CAP_FACE",FACE,{"disambiguationData":[OSD([subQ8,subQ7,subQ6,subQ5,subQ4,subQ3,subQ2,subQ1,subQ0]),ownerDisambiguation([makeQuery(id+"F4.opExtrude","SWEPT_BODY",BODY,{"disambiguationData":[OSD([sQuery(id+"F3.wireOp",EDGE,"E27.15.0"),sQuery(id+"F3.wireOp",EDGE,"E27.15.1"),sQuery(id+"F3.wireOp",EDGE,"E27.15.2"),sQuery(id+"F3.wireOp",EDGE,"E27.15.3")])]})])],"isStart":false}),makeQuery(id+"F4.opExtrude","CAP_FACE",FACE,{"disambiguationData":[OSD([subQ8,subQ7,subQ6,subQ5,subQ4,subQ3,subQ2,subQ1,subQ0]),ownerDisambiguation([makeQuery(id+"F4.opExtrude","SWEPT_BODY",BODY,{"disambiguationData":[OSD([sQuery(id+"F3.wireOp",EDGE,"E27.16.0"),sQuery(id+"F3.wireOp",EDGE,"E27.16.1"),sQuery(id+"F3.wireOp",EDGE,"E27.16.2"),sQuery(id+"F3.wireOp",EDGE,"E27.16.3")])]})])],"isStart":false}),makeQuery(id+"F4.opExtrude","CAP_FACE",FACE,{"disambiguationData":[OSD([subQ8,subQ7,subQ6,subQ5,subQ4,subQ3,subQ2,subQ1,subQ0]),ownerDisambiguation([makeQuery(id+"F4.opExtrude","SWEPT_BODY",BODY,{"disambiguationData":[OSD([sQuery(id+"F3.wireOp",EDGE,"E27.17.0"),sQuery(id+"F3.wireOp",EDGE,"E27.17.1"),sQuery(id+"F3.wireOp",EDGE,"E27.17.2"),sQuery(id+"F3.wireOp",EDGE,"E27.17.3")])]})])],"isStart":false}),makeQuery(id+"F4.opExtrude","CAP_FACE",FACE,{"disambiguationData":[OSD([subQ8,subQ7,subQ6,subQ5,subQ4,subQ3,subQ2,subQ1,subQ0]),ownerDisambiguation([makeQuery(id+"F4.opExtrude","SWEPT_BODY",BODY,{"disambiguationData":[OSD([sQuery(id+"F3.wireOp",EDGE,"E27.18.0"),sQuery(id+"F3.wireOp",EDGE,"E27.18.1"),sQuery(id+"F3.wireOp",EDGE,"E27.18.2"),sQuery(id+"F3.wireOp",EDGE,"E27.18.3")])]})])],"isStart":false}),makeQuery(id+"F4.opExtrude","CAP_FACE",FACE,{"disambiguationData":[OSD([subQ8,subQ7,subQ6,subQ5,subQ4,subQ3,subQ2,subQ1,subQ0]),ownerDisambiguation([makeQuery(id+"F4.opExtrude","SWEPT_BODY",BODY,{"disambiguationData":[OSD([sQuery(id+"F3.wireOp",EDGE,"E27.19.0"),sQuery(id+"F3.wireOp",EDGE,"E27.19.1"),sQuery(id+"F3.wireOp",EDGE,"E27.19.2"),sQuery(id+"F3.wireOp",EDGE,"E27.19.3")])]})])],"isStart":false}),makeQuery(id+"F4.opExtrude","CAP_FACE",FACE,{"disambiguationData":[OSD([subQ8,subQ7,subQ6,subQ5,subQ4,subQ3,subQ2,subQ1,subQ0]),ownerDisambiguation([makeQuery(id+"F4.opExtrude","SWEPT_BODY",BODY,{"disambiguationData":[OSD([sQuery(id+"F3.wireOp",EDGE,"E27.20.0"),sQuery(id+"F3.wireOp",EDGE,"E27.20.1"),sQuery(id+"F3.wireOp",EDGE,"E27.20.2"),sQuery(id+"F3.wireOp",EDGE,"E27.20.3")])]})])],"isStart":false}),makeQuery(id+"F4.opExtrude","CAP_FACE",FACE,{"disambiguationData":[OSD([subQ8,subQ7,subQ6,subQ5,subQ4,subQ3,subQ2,subQ1,subQ0]),ownerDisambiguation([makeQuery(id+"F4.opExtrude","SWEPT_BODY",BODY,{"disambiguationData":[OSD([sQuery(id+"F3.wireOp",EDGE,"E27.21.0"),sQuery(id+"F3.wireOp",EDGE,"E27.21.1"),sQuery(id+"F3.wireOp",EDGE,"E27.21.2"),sQuery(id+"F3.wireOp",EDGE,"E27.21.3")])]})])],"isStart":false}),makeQuery(id+"F4.opExtrude","CAP_FACE",FACE,{"disambiguationData":[OSD([subQ8,subQ7,subQ6,subQ5,subQ4,subQ3,subQ2,subQ1,subQ0]),ownerDisambiguation([makeQuery(id+"F4.opExtrude","SWEPT_BODY",BODY,{"disambiguationData":[OSD([sQuery(id+"F3.wireOp",EDGE,"E27.22.0"),sQuery(id+"F3.wireOp",EDGE,"E27.22.1"),sQuery(id+"F3.wireOp",EDGE,"E27.22.2"),sQuery(id+"F3.wireOp",EDGE,"E27.22.3")])]})])],"isStart":false}),makeQuery(id+"F4.opExtrude","CAP_FACE",FACE,{"disambiguationData":[OSD([subQ8,subQ7,subQ6,subQ5,subQ4,subQ3,subQ2,subQ1,subQ0]),ownerDisambiguation([makeQuery(id+"F4.opExtrude","SWEPT_BODY",BODY,{"disambiguationData":[OSD([sQuery(id+"F3.wireOp",EDGE,"E27.23.0"),sQuery(id+"F3.wireOp",EDGE,"E27.23.1"),sQuery(id+"F3.wireOp",EDGE,"E27.23.2"),sQuery(id+"F3.wireOp",EDGE,"E27.23.3")])]})])],"isStart":false}),makeQuery(id+"F4.opExtrude","CAP_FACE",FACE,{"disambiguationData":[OSD([subQ8,subQ7,subQ6,subQ5,subQ4,subQ3,subQ2,subQ1,subQ0]),ownerDisambiguation([makeQuery(id+"F4.opExtrude","SWEPT_BODY",BODY,{"disambiguationData":[OSD([sQuery(id+"F3.wireOp",EDGE,"E27.24.0"),sQuery(id+"F3.wireOp",EDGE,"E27.24.1"),sQuery(id+"F3.wireOp",EDGE,"E27.24.2"),sQuery(id+"F3.wireOp",EDGE,"E27.24.3")])]})])],"isStart":false}),makeQuery(id+"F4.opExtrude","CAP_FACE",FACE,{"disambiguationData":[OSD([subQ8,subQ7,subQ6,subQ5,subQ4,subQ3,subQ2,subQ1,subQ0]),ownerDisambiguation([makeQuery(id+"F4.opExtrude","SWEPT_BODY",BODY,{"disambiguationData":[OSD([sQuery(id+"F3.wireOp",EDGE,"E27.25.0"),sQuery(id+"F3.wireOp",EDGE,"E27.25.1"),sQuery(id+"F3.wireOp",EDGE,"E27.25.2"),sQuery(id+"F3.wireOp",EDGE,"E27.25.3")])]})])],"isStart":false}),makeQuery(id+"F4.opExtrude","CAP_FACE",FACE,{"disambiguationData":[OSD([subQ8,subQ7,subQ6,subQ5,subQ4,subQ3,subQ2,subQ1,subQ0]),ownerDisambiguation([makeQuery(id+"F4.opExtrude","SWEPT_BODY",BODY,{"disambiguationData":[OSD([sQuery(id+"F3.wireOp",EDGE,"E27.26.0"),sQuery(id+"F3.wireOp",EDGE,"E27.26.1"),sQuery(id+"F3.wireOp",EDGE,"E27.26.2"),sQuery(id+"F3.wireOp",EDGE,"E27.26.3")])]})])],"isStart":false}),makeQuery(id+"F4.opExtrude","CAP_FACE",FACE,{"disambiguationData":[OSD([subQ8,subQ7,subQ6,subQ5,subQ4,subQ3,subQ2,subQ1,subQ0]),ownerDisambiguation([makeQuery(id+"F4.opExtrude","SWEPT_BODY",BODY,{"disambiguationData":[OSD([sQuery(id+"F3.wireOp",EDGE,"E27.27.0"),sQuery(id+"F3.wireOp",EDGE,"E27.27.1"),sQuery(id+"F3.wireOp",EDGE,"E27.27.2"),sQuery(id+"F3.wireOp",EDGE,"E27.27.3")])]})])],"isStart":false}),makeQuery(id+"F4.opExtrude","CAP_FACE",FACE,{"disambiguationData":[OSD([subQ8,subQ7,subQ6,subQ5,subQ4,subQ3,subQ2,subQ1,subQ0]),ownerDisambiguation([makeQuery(id+"F4.opExtrude","SWEPT_BODY",BODY,{"disambiguationData":[OSD([sQuery(id+"F3.wireOp",EDGE,"E27.28.0"),sQuery(id+"F3.wireOp",EDGE,"E27.28.1"),sQuery(id+"F3.wireOp",EDGE,"E27.28.2"),sQuery(id+"F3.wireOp",EDGE,"E27.28.3")])]})])],"isStart":false}),makeQuery(id+"F4.opExtrude","CAP_FACE",FACE,{"disambiguationData":[OSD([subQ8,subQ7,subQ6,subQ5,subQ4,subQ3,subQ2,subQ1,subQ0]),ownerDisambiguation([makeQuery(id+"F4.opExtrude","SWEPT_BODY",BODY,{"disambiguationData":[OSD([sQuery(id+"F3.wireOp",EDGE,"E27.29.0"),sQuery(id+"F3.wireOp",EDGE,"E27.29.1"),sQuery(id+"F3.wireOp",EDGE,"E27.29.2"),sQuery(id+"F3.wireOp",EDGE,"E27.29.3")])]})])],"isStart":false}),makeQuery(id+"F4.opExtrude","CAP_FACE",FACE,{"disambiguationData":[OSD([subQ8,subQ7,subQ6,subQ5,subQ4,subQ3,subQ2,subQ1,subQ0]),ownerDisambiguation([makeQuery(id+"F4.opExtrude","SWEPT_BODY",BODY,{"disambiguationData":[OSD([sQuery(id+"F3.wireOp",EDGE,"E27.30.0"),sQuery(id+"F3.wireOp",EDGE,"E27.30.1"),sQuery(id+"F3.wireOp",EDGE,"E27.30.2"),sQuery(id+"F3.wireOp",EDGE,"E27.30.3")])]})])],"isStart":false}),makeQuery(id+"F4.opExtrude","CAP_FACE",FACE,{"disambiguationData":[OSD([subQ8,subQ7,subQ6,subQ5,subQ4,subQ3,subQ2,subQ1,subQ0]),ownerDisambiguation([makeQuery(id+"F4.opExtrude","SWEPT_BODY",BODY,{"disambiguationData":[OSD([sQuery(id+"F3.wireOp",EDGE,"E27.31.0"),sQuery(id+"F3.wireOp",EDGE,"E27.31.1"),sQuery(id+"F3.wireOp",EDGE,"E27.31.2"),sQuery(id+"F3.wireOp",EDGE,"E27.31.3")])]})])],"isStart":false}),makeQuery(id+"F4.opExtrude","CAP_FACE",FACE,{"disambiguationData":[OSD([subQ8,subQ7,subQ6,subQ5,subQ4,subQ3,subQ2,subQ1,subQ0]),ownerDisambiguation([makeQuery(id+"F4.opExtrude","SWEPT_BODY",BODY,{"disambiguationData":[OSD([sQuery(id+"F3.wireOp",EDGE,"E27.32.0"),sQuery(id+"F3.wireOp",EDGE,"E27.32.1"),sQuery(id+"F3.wireOp",EDGE,"E27.32.2"),sQuery(id+"F3.wireOp",EDGE,"E27.32.3")])]})])],"isStart":false}),makeQuery(id+"F4.opExtrude","CAP_FACE",FACE,{"disambiguationData":[OSD([subQ8,subQ7,subQ6,subQ5,subQ4,subQ3,subQ2,subQ1,subQ0]),ownerDisambiguation([makeQuery(id+"F4.opExtrude","SWEPT_BODY",BODY,{"disambiguationData":[OSD([sQuery(id+"F3.wireOp",EDGE,"E27.33.0"),sQuery(id+"F3.wireOp",EDGE,"E27.33.1"),sQuery(id+"F3.wireOp",EDGE,"E27.33.2"),sQuery(id+"F3.wireOp",EDGE,"E27.33.3")])]})])],"isStart":false}),makeQuery(id+"F4.opExtrude","CAP_FACE",FACE,{"disambiguationData":[OSD([subQ8,subQ7,subQ6,subQ5,subQ4,subQ3,subQ2,subQ1,subQ0]),ownerDisambiguation([makeQuery(id+"F4.opExtrude","SWEPT_BODY",BODY,{"disambiguationData":[OSD([sQuery(id+"F3.wireOp",EDGE,"E27.34.0"),sQuery(id+"F3.wireOp",EDGE,"E27.34.1"),sQuery(id+"F3.wireOp",EDGE,"E27.34.2"),sQuery(id+"F3.wireOp",EDGE,"E27.34.3")])]})])],"isStart":false}),makeQuery(id+"F4.opExtrude","CAP_FACE",FACE,{"disambiguationData":[OSD([subQ8,subQ7,subQ6,subQ5,subQ4,subQ3,subQ2,subQ1,subQ0]),ownerDisambiguation([makeQuery(id+"F4.opExtrude","SWEPT_BODY",BODY,{"disambiguationData":[OSD([sQuery(id+"F3.wireOp",EDGE,"E27.35.0"),sQuery(id+"F3.wireOp",EDGE,"E27.35.1"),sQuery(id+"F3.wireOp",EDGE,"E27.35.2"),sQuery(id+"F3.wireOp",EDGE,"E27.35.3")])]})])],"isStart":false}),makeQuery(id+"F4.opExtrude","CAP_FACE",FACE,{"disambiguationData":[OSD([subQ8,subQ7,subQ6,subQ5,subQ4,subQ3,subQ2,subQ1,subQ0]),ownerDisambiguation([makeQuery(id+"F4.opExtrude","SWEPT_BODY",BODY,{"disambiguationData":[OSD([sQuery(id+"F3.wireOp",EDGE,"E27.36.0"),sQuery(id+"F3.wireOp",EDGE,"E27.36.1"),sQuery(id+"F3.wireOp",EDGE,"E27.36.2"),sQuery(id+"F3.wireOp",EDGE,"E27.36.3")])]})])],"isStart":false}),makeQuery(id+"F4.opExtrude","CAP_FACE",FACE,{"disambiguationData":[OSD([subQ8,subQ7,subQ6,subQ5,subQ4,subQ3,subQ2,subQ1,subQ0]),ownerDisambiguation([makeQuery(id+"F4.opExtrude","SWEPT_BODY",BODY,{"disambiguationData":[OSD([sQuery(id+"F3.wireOp",EDGE,"E27.37.0"),sQuery(id+"F3.wireOp",EDGE,"E27.37.1"),sQuery(id+"F3.wireOp",EDGE,"E27.37.2"),sQuery(id+"F3.wireOp",EDGE,"E27.37.3")])]})])],"isStart":false}),makeQuery(id+"F4.opExtrude","CAP_FACE",FACE,{"disambiguationData":[OSD([subQ8,subQ7,subQ6,subQ5,subQ4,subQ3,subQ2,subQ1,subQ0]),ownerDisambiguation([makeQuery(id+"F4.opExtrude","SWEPT_BODY",BODY,{"disambiguationData":[OSD([sQuery(id+"F3.wireOp",EDGE,"E27.38.0"),sQuery(id+"F3.wireOp",EDGE,"E27.38.1"),sQuery(id+"F3.wireOp",EDGE,"E27.38.2"),sQuery(id+"F3.wireOp",EDGE,"E27.38.3")])]})])],"isStart":false}),makeQuery(id+"F4.opExtrude","CAP_FACE",FACE,{"disambiguationData":[OSD([subQ8,subQ7,subQ6,subQ5,subQ4,subQ3,subQ2,subQ1,subQ0]),ownerDisambiguation([makeQuery(id+"F4.opExtrude","SWEPT_BODY",BODY,{"disambiguationData":[OSD([sQuery(id+"F3.wireOp",EDGE,"E27.39.0"),sQuery(id+"F3.wireOp",EDGE,"E27.39.1"),sQuery(id+"F3.wireOp",EDGE,"E27.39.2"),sQuery(id+"F3.wireOp",EDGE,"E27.39.3")])]})])],"isStart":false}),makeQuery(id+"F4.opExtrude","CAP_FACE",FACE,{"disambiguationData":[OSD([subQ8,subQ7,subQ6,subQ5,subQ4,subQ3,subQ2,subQ1,subQ0]),ownerDisambiguation([makeQuery(id+"F4.opExtrude","SWEPT_BODY",BODY,{"disambiguationData":[OSD([sQuery(id+"F3.wireOp",EDGE,"E27.40.0"),sQuery(id+"F3.wireOp",EDGE,"E27.40.1"),sQuery(id+"F3.wireOp",EDGE,"E27.40.2"),sQuery(id+"F3.wireOp",EDGE,"E27.40.3")])]})])],"isStart":false}),makeQuery(id+"F4.opExtrude","CAP_FACE",FACE,{"disambiguationData":[OSD([subQ8,subQ7,subQ6,subQ5,subQ4,subQ3,subQ2,subQ1,subQ0]),ownerDisambiguation([makeQuery(id+"F4.opExtrude","SWEPT_BODY",BODY,{"disambiguationData":[OSD([sQuery(id+"F3.wireOp",EDGE,"E27.41.0"),sQuery(id+"F3.wireOp",EDGE,"E27.41.1"),sQuery(id+"F3.wireOp",EDGE,"E27.41.2"),sQuery(id+"F3.wireOp",EDGE,"E27.41.3")])]})])],"isStart":false}),makeQuery(id+"F4.opExtrude","CAP_FACE",FACE,{"disambiguationData":[OSD([subQ8,subQ7,subQ6,subQ5,subQ4,subQ3,subQ2,subQ1,subQ0]),ownerDisambiguation([makeQuery(id+"F4.opExtrude","SWEPT_BODY",BODY,{"disambiguationData":[OSD([sQuery(id+"F3.wireOp",EDGE,"E27.42.0"),sQuery(id+"F3.wireOp",EDGE,"E27.42.1"),sQuery(id+"F3.wireOp",EDGE,"E27.42.2"),sQuery(id+"F3.wireOp",EDGE,"E27.42.3")])]})])],"isStart":false}),makeQuery(id+"F4.opExtrude","CAP_FACE",FACE,{"disambiguationData":[OSD([subQ8,subQ7,subQ6,subQ5,subQ4,subQ3,subQ2,subQ1,subQ0]),ownerDisambiguation([makeQuery(id+"F4.opExtrude","SWEPT_BODY",BODY,{"disambiguationData":[OSD([sQuery(id+"F3.wireOp",EDGE,"E27.43.0"),sQuery(id+"F3.wireOp",EDGE,"E27.43.1"),sQuery(id+"F3.wireOp",EDGE,"E27.43.2"),sQuery(id+"F3.wireOp",EDGE,"E27.43.3")])]})])],"isStart":false}),makeQuery(id+"F4.opExtrude","CAP_FACE",FACE,{"disambiguationData":[OSD([subQ8,subQ7,subQ6,subQ5,subQ4,subQ3,subQ2,subQ1,subQ0]),ownerDisambiguation([makeQuery(id+"F4.opExtrude","SWEPT_BODY",BODY,{"disambiguationData":[OSD([sQuery(id+"F3.wireOp",EDGE,"E27.44.0"),sQuery(id+"F3.wireOp",EDGE,"E27.44.1"),sQuery(id+"F3.wireOp",EDGE,"E27.44.2"),sQuery(id+"F3.wireOp",EDGE,"E27.44.3")])]})])],"isStart":false}),makeQuery(id+"F4.opExtrude","CAP_FACE",FACE,{"disambiguationData":[OSD([subQ8,subQ7,subQ6,subQ5,subQ4,subQ3,subQ2,subQ1,subQ0]),ownerDisambiguation([makeQuery(id+"F4.opExtrude","SWEPT_BODY",BODY,{"disambiguationData":[OSD([sQuery(id+"F3.wireOp",EDGE,"E27.45.0"),sQuery(id+"F3.wireOp",EDGE,"E27.45.1"),sQuery(id+"F3.wireOp",EDGE,"E27.45.2"),sQuery(id+"F3.wireOp",EDGE,"E27.45.3")])]})])],"isStart":false}),makeQuery(id+"F4.opExtrude","CAP_FACE",FACE,{"disambiguationData":[OSD([subQ8,subQ7,subQ6,subQ5,subQ4,subQ3,subQ2,subQ1,subQ0]),ownerDisambiguation([makeQuery(id+"F4.opExtrude","SWEPT_BODY",BODY,{"disambiguationData":[OSD([sQuery(id+"F3.wireOp",EDGE,"E27.46.0"),sQuery(id+"F3.wireOp",EDGE,"E27.46.1"),sQuery(id+"F3.wireOp",EDGE,"E27.46.2"),sQuery(id+"F3.wireOp",EDGE,"E27.46.3")])]})])],"isStart":false}),makeQuery(id+"F4.opExtrude","CAP_FACE",FACE,{"disambiguationData":[OSD([subQ8,subQ7,subQ6,subQ5,subQ4,subQ3,subQ2,subQ1,subQ0]),ownerDisambiguation([makeQuery(id+"F4.opExtrude","SWEPT_BODY",BODY,{"disambiguationData":[OSD([sQuery(id+"F3.wireOp",EDGE,"E27.47.0"),sQuery(id+"F3.wireOp",EDGE,"E27.47.1"),sQuery(id+"F3.wireOp",EDGE,"E27.47.2"),sQuery(id+"F3.wireOp",EDGE,"E27.47.3")])]})])],"isStart":false})]});}
            extrude(context, id + "F7", {"entities" : qUnion([Q0]), "endBound" : BoundingType.UP_TO_SURFACE, "oppositeDirection" : true, "endBoundEntityFace" : qUnion([Q1]), "depth" : 25.4 * mm, "hasSecondDirection" : true, "secondDirectionBound" : SecondDirectionBoundingType.UP_TO_SURFACE, "secondDirectionOppositeDirection" : false, "secondDirectionBoundEntityFace" : qUnion([Q2]), "secondDirectionDepth" : 25.4 * mm});
        }
        {
            var Q0;
            Q0=makeQuery(id+"F7.opExtrude","SWEPT_BODY",BODY,{"disambiguationData":[OSD([sQuery(id+"F6.wireOp",EDGE,"E34.0"),sQuery(id+"F6.wireOp",EDGE,"E35"),sQuery(id+"F6.wireOp",EDGE,"mRtnFgvG-hzmj-HngR-CWAN-6ifdWNZuS1hl"),sQuery(id+"F6.wireOp",EDGE,"E38.MirrorCS")])]});
            var Q1;
            Q1=makeQuery(id+"F7.opExtrude","SWEPT_FACE",FACE,{"disambiguationData":[OSD([sQuery(id+"F6.wireOp",EDGE,"E34.0")])]});
            circularPattern(context, id + "F8", {"entities" : qUnion([Q0]), "axis" : qUnion([Q1]), "angle" : 360 * degree, "instanceCount" : 8, "equalSpace" : true});
        }
    });
